FCSTD DOCUMENT  (FreeCAD 0.19R24291 (Git))
Label: assembly
License: All rights reserved
LicenseURL: http://en.wikipedia.org/wiki/All_rights_reserved
objects: App::Link×9, App::DocumentObjectGroup×3, PartDesign::CoordinateSystem×1, App::FeaturePython×1, App::Part×1
note: 1 computed .brp shape members not serialized (recipe doc carries the construction recipe); baked Part::Feature solids carry a one-line shape summary decoded from their .brp
EXTERNAL_REF file=Back.FCStd obj=LCS_0
EXTERNAL_REF file=Back.FCStd obj=Body_back
EXTERNAL_REF file=Back.FCStd obj=LCS_gear02
EXTERNAL_REF file=Gear02.FCStd obj=LCS_0
EXTERNAL_REF file=Gear02.FCStd obj=Part_gear02
EXTERNAL_REF file=Back.FCStd obj=LCS_stepper_mount_1
EXTERNAL_REF file=Stepper28BYJ48.FCStd obj=LCS_mount2
EXTERNAL_REF file=Stepper28BYJ48.FCStd obj=Part_Stepper28BYJ48
EXTERNAL_REF file=Gear01.FCStd obj=LCS_0
EXTERNAL_REF file=Stepper28BYJ48.FCStd obj=LCS_gear01
EXTERNAL_REF file=Gear01.FCStd obj=Part_gear01
EXTERNAL_REF file=Back.FCStd obj=LCS_spacer
EXTERNAL_REF file=Gear02Cap.FCStd obj=LCS_0
EXTERNAL_REF file=Gear02Cap.FCStd obj=Body_gear02cap
EXTERNAL_REF file=Back.FCStd obj=LCS_lcd
EXTERNAL_REF file=LCD114.FCStd obj=LCS_mount
EXTERNAL_REF file=LCD114.FCStd obj=Body_lcd1_14
EXTERNAL_REF file=Back.FCStd obj=LCS_pcb_1
EXTERNAL_REF file=PCB.FCStd obj=LCS_0
EXTERNAL_REF file=PCB.FCStd obj=Board_18fc
EXTERNAL_REF file=Back.FCStd obj=LCS_front
EXTERNAL_REF file=Front.FCStd obj=LCS_back
EXTERNAL_REF file=Front.FCStd obj=Body_front
EXTERNAL_REF file=PCB.FCStd obj=LCS_knob
EXTERNAL_REF file=knob.FCStd obj=LCS_encoder
EXTERNAL_REF file=knob.FCStd obj=Body_knob

FEATURE [App::DocumentObjectGroup] Parts
FEATURE [PartDesign::CoordinateSystem] LCS_Origin
  AttacherType = Attacher::AttachEngine3D
  MapMode = 2
  Support = -> [X_Axis]
FEATURE [App::FeaturePython] Variables  # WARN: FeaturePython — macro-defined, semantics opaque (R4)
  Type = App::PropertyContainer
FEATURE [App::DocumentObjectGroup] Constraints
FEATURE [App::DocumentObjectGroup] Configurations
FEATURE [App::Link] Body_back
  AttachedBy = #LCS_0
  AttachedTo = Parent Assembly#LCS_Origin
  LinkedObject = -> <external Back.FCStd>#Body_back
  SolverId = Placement::ExpressionEngine
  expr: Placement = LCS_Origin.Placement * AttachmentOffset * Back#LCS_0.Placement ^ -1
FEATURE [App::Link] Part_gear02
  AttachedBy = #LCS_0
  AttachedTo = Body_back#LCS_gear02
  AttachmentOffset = pos=(0,0,0) rot=(0,0,1;3.14159rad)
  LinkPlacement = pos=(17.15,53,27.8) rot=(0,0,1;4.71239rad)
  LinkedObject = -> <external Gear02.FCStd>#Part_gear02
  Placement = pos=(17.15,53,27.8) rot=(0,0,1;4.71239rad)
  SolverId = Placement::ExpressionEngine
  expr: Placement = Body_back.Placement * Back#LCS_gear02.Placement * AttachmentOffset * Gear02#LCS_0.Placement ^ -1
FEATURE [App::Link] Part_Stepper28BYJ48
  AttachedBy = #LCS_mount2
  AttachedTo = Body_back#LCS_stepper_mount_1
  AttachmentOffset = pos=(0,0,0) rot=(0.707107,0.707107,0;3.14159rad)
  LinkPlacement = pos=(-13.35,53,6.9) rot=(-0.57735,0.57735,0.57735;4.18879rad)
  LinkedObject = -> <external Stepper28BYJ48.FCStd>#Part_Stepper28BYJ48
  Placement = pos=(-13.35,53,6.9) rot=(-0.57735,0.57735,0.57735;4.18879rad)
  SolverId = Placement::ExpressionEngine
  expr: Placement = Body_back.Placement * Back#LCS_stepper_mount_1.Placement * AttachmentOffset * Stepper28BYJ48#LCS_mount2.Placement ^ -1
FEATURE [App::Link] Part_gear01
  AttachedBy = #LCS_0
  AttachedTo = Part_Stepper28BYJ48#LCS_gear01
  AttachmentOffset = pos=(0,0,0) rot=(0,0,1;1.5708rad)
  LinkPlacement = pos=(-5.35,53,27.4) rot=(0,0,1;0rad)
  LinkedObject = -> <external Gear01.FCStd>#Part_gear01
  Placement = pos=(-5.35,53,27.4) rot=(0,0,1;0rad)
  SolverId = Placement::ExpressionEngine
  expr: Placement = Part_Stepper28BYJ48.Placement * Stepper28BYJ48#LCS_gear01.Placement * AttachmentOffset * Gear01#LCS_0.Placement ^ -1
FEATURE [App::Link] Body_gear02cap
  AttachedBy = #LCS_0
  AttachedTo = Body_back#LCS_spacer
  LinkPlacement = pos=(17.15,53,35) rot=(0,0,1;1.5708rad)
  LinkedObject = -> <external Gear02Cap.FCStd>#Body_gear02cap
  Placement = pos=(17.15,53,35) rot=(0,0,1;1.5708rad)
  SolverId = Placement::ExpressionEngine
  expr: Placement = Body_back.Placement * Back#LCS_spacer.Placement * AttachmentOffset * Gear02Cap#LCS_0.Placement ^ -1
FEATURE [App::Link] Body_LCD114
  AttachedBy = #LCS_mount
  AttachedTo = Body_back#LCS_lcd
  AttachmentOffset = pos=(0,0,0) rot=(0,0,1;3.14159rad)
  LinkPlacement = pos=(-5.3e-15,-58.5,46.25) rot=(0,0,1;3.14159rad)
  LinkedObject = -> <external LCD114.FCStd>#Body_lcd1_14
  Placement = pos=(-5.3e-15,-58.5,46.25) rot=(0,0,1;3.14159rad)
  SolverId = Placement::ExpressionEngine
  expr: Placement = Body_back.Placement * Back#LCS_lcd.Placement * AttachmentOffset * LCD114#LCS_mount.Placement ^ -1
FEATURE [App::Link] PCB
  AttachedBy = #LCS_0
  AttachedTo = Body_back#LCS_pcb_1
  LinkPlacement = pos=(-39.15,-25.3,38.6) rot=(0,0,1;0rad)
  LinkedObject = -> <external PCB.FCStd>#Board_18fc
  Placement = pos=(-39.15,-25.3,38.6) rot=(0,0,1;0rad)
  SolverId = Placement::ExpressionEngine
  expr: Placement = Body_back.Placement * Back#LCS_pcb_1.Placement * AttachmentOffset * PCB#LCS_0.Placement ^ -1
FEATURE [App::Link] Body_front
  AttachedBy = #LCS_back
  AttachedTo = Body_back#LCS_front
  AttachmentOffset = pos=(0,0,0) rot=(0,0,1;3.14159rad)
  LinkPlacement = pos=(-1.066e-13,2.487e-13,49.6) rot=(0,0,1;0rad)
  LinkedObject = -> <external Front.FCStd>#Body_front
  Placement = pos=(-1.066e-13,2.487e-13,49.6) rot=(0,0,1;0rad)
  SolverId = Placement::ExpressionEngine
  expr: Placement = Body_back.Placement * Back#LCS_front.Placement * AttachmentOffset * Front#LCS_back.Placement ^ -1
FEATURE [App::Link] Body_knob
  AttachedBy = #LCS_encoder
  AttachedTo = PCB#LCS_knob
  AttachmentOffset = pos=(0,0,0) rot=(1,0,0;3.14159rad)
  LinkPlacement = pos=(-7.05,1.6,46.4) rot=(0,0,1;3.72602rad)
  LinkedObject = -> <external knob.FCStd>#Body_knob
  Placement = pos=(-7.05,1.6,46.4) rot=(0,0,1;3.72602rad)
  SolverId = Placement::ExpressionEngine
  expr: Placement = PCB.Placement * PCB#LCS_knob.Placement * AttachmentOffset * knob#LCS_encoder.Placement ^ -1
FEATURE [App::Part] Assembly
  AssemblyType = Part::Link
  Group = -> [LCS_Origin,Variables,Constraints,Configurations,Body_back,Part_gear02,Part_Stepper28BYJ48,Part_gear01,Body_gear02cap,Body_LCD114,PCB,Body_front,Body_knob]
  Origin = -> Origin
  Type = Assembly

RESOLVED EXTERNAL PARTS (link-assembly join: the EXTERNAL_REF files above that resolve inside this repo's crawl, each included once):
---- part Back.FCStd = doc fcstd_51bf11bdf407 ----
FCSTD DOCUMENT  (FreeCAD 0.19R24291 (Git))
Label: Back
License: All rights reserved
LicenseURL: http://en.wikipedia.org/wiki/All_rights_reserved
objects: Sketcher::SketchObject×9, PartDesign::Pad×9, PartDesign::CoordinateSystem×7, PartDesign::Fillet×1, PartDesign::Body×1
note: 37 computed .brp shape members not serialized (recipe doc carries the construction recipe); baked Part::Feature solids carry a one-line shape summary decoded from their .brp
EXTERNAL_REF file=data.FCStd obj=Spreadsheet

FEATURE [PartDesign::CoordinateSystem] LCS_0
  AttacherType = Attacher::AttachEngine3D
  MapMode = 2
  Support = -> [X_Axis]
FEATURE [Sketcher::SketchObject] Sketch  label="Sketch_back"
  FullyConstrained = true
  MapMode = 5
  Support = -> [XY_Plane]
  expr: Constraints[27] = data#<<data>>.OutsideLength
  expr: Constraints[28] = data#<<data>>.OutsideRadius
  expr: Constraints[26] = data#<<data>>.OutsideWidth
  expr: Constraints[25] = data#<<data>>.OutsideCornerRadius
  sketch-geometry (12):
    g0: ArcOfCircle CenterX=-37.75 CenterY=73.6 CenterZ=0 NormalX=0 NormalY=0 NormalZ=1 AngleXU=0 Radius=4.8 StartAngle=1.5708 EndAngle=3.14159
    g1: ArcOfCircle CenterX=17.15 CenterY=53 CenterZ=0 NormalX=0 NormalY=0 NormalZ=1 AngleXU=0 Radius=25.4 StartAngle=0 EndAngle=1.5708
    g2: ArcOfCircle CenterX=37.75 CenterY=-73.6 CenterZ=0 NormalX=0 NormalY=0 NormalZ=1 AngleXU=0 Radius=4.8 StartAngle=4.71239 EndAngle=6.28319
    g3: ArcOfCircle CenterX=-37.75 CenterY=-73.6 CenterZ=0 NormalX=0 NormalY=0 NormalZ=1 AngleXU=0 Radius=4.8 StartAngle=3.14159 EndAngle=4.71239
    g4: LineSegment StartX=-42.55 StartY=73.6 StartZ=0 EndX=-42.55 EndY=78.4 EndZ=0
    g5: LineSegment StartX=-37.75 StartY=78.4 StartZ=0 EndX=-42.55 EndY=78.4 EndZ=0
    g6: LineSegment StartX=37.75 StartY=-78.4 StartZ=0 EndX=42.55 EndY=-78.4 EndZ=0
    g7: LineSegment StartX=42.55 StartY=-73.6 StartZ=0 EndX=42.55 EndY=-78.4 EndZ=0
    g8: LineSegment StartX=-42.55 StartY=73.6 StartZ=0 EndX=-42.55 EndY=-73.6 EndZ=0
    g9: LineSegment StartX=-37.75 StartY=78.4 StartZ=0 EndX=17.15 EndY=78.4 EndZ=0
    g10: LineSegment StartX=42.55 StartY=53 StartZ=0 EndX=42.55 EndY=-73.6 EndZ=0
    g11: LineSegment StartX=-37.75 StartY=-78.4 StartZ=0 EndX=37.75 EndY=-78.4 EndZ=0
  constraints (37):
    c: Equal(g0,g3)
    c: Equal(g3,g2)
    c: Vertical(g0,g0)
    c: Vertical(g3,g3)
    c: Vertical(g2,g2)
    c: Vertical(g1,g1)
    c: Horizontal(g0,g0)
    c: Horizontal(g1,g1)
    c: Horizontal(g2,g2)
    c: Horizontal(g3,g3)
    c: Vertical(g0,g3)
    c: Vertical(g1,g2)
    c: Horizontal(g0,g1)
    c: Horizontal(g3,g2)
    c: Coincident(g4,g0)
    c: Vertical(g4)
    c: Coincident(g5,g0)
    c: Horizontal(g5)
    c: Coincident(g6,g2)
    c: Horizontal(g6)
    c: Coincident(g7,g2)
    c: Vertical(g7)
    c: Coincident(g5,g4)
    c: Coincident(g7,g6)
    c: Symmetric(g4,g6,g-1)
    c: Radius(g3) = 4.8
    c: DistanceX(g4,g1) = 85.1
    c: DistanceY(g3,g4) = 156.8
    c: Radius(g1) = 25.4
    c: Coincident(g8,g0)
    c: Coincident(g9,g0)
    c: Coincident(g10,g1)
    c: Coincident(g11,g3)
    c: Coincident(g11,g2)
    c: Coincident(g2,g10)
    c: Coincident(g8,g3)
    c: Coincident(g9,g1)
FEATURE [PartDesign::Pad] Pad
  Direction = (1,1,1)
  Length = 2.4
  Length2 = 100
  Profile = -> Sketch
  Type = 0
  expr: Length = data#<<data>>.WallThickness
FEATURE [Sketcher::SketchObject] Sketch001  label="Sketch_wall1"
  AttachmentOffset = pos=(0,0,2.4) rot=(0,0,1;0rad)
  FullyConstrained = true
  MapMode = 5
  Placement = pos=(0,0,2.4) rot=(0,0,1;0rad)
  Support = -> [XY_Plane]
  expr: Constraints[48] = data#<<data>>.InsideRadius
  expr: Constraints[47] = data#<<data>>.InsideCornerRadius
  expr: .AttachmentOffset.Base.z = data#<<data>>.WallThickness
  expr: Constraints[24] = data#<<data>>.OutsideWidth
  expr: Constraints[22] = data#<<data>>.OutsideRadius
  expr: Constraints[23] = data#<<data>>.OutsideLength
  expr: Constraints[21] = data#<<data>>.OutsideCornerRadius
  sketch-geometry (20):
    g0: ArcOfCircle CenterX=-37.75 CenterY=73.6 CenterZ=0 NormalX=0 NormalY=0 NormalZ=1 AngleXU=0 Radius=4.8 StartAngle=1.5708 EndAngle=3.14159
    g1: ArcOfCircle CenterX=17.15 CenterY=53 CenterZ=0 NormalX=0 NormalY=0 NormalZ=1 AngleXU=0 Radius=25.4 StartAngle=0 EndAngle=1.5708
    g2: ArcOfCircle CenterX=37.75 CenterY=-73.6 CenterZ=0 NormalX=0 NormalY=0 NormalZ=1 AngleXU=0 Radius=4.8 StartAngle=4.71239 EndAngle=6.28319
    g3: ArcOfCircle CenterX=-37.75 CenterY=-73.6 CenterZ=0 NormalX=0 NormalY=0 NormalZ=1 AngleXU=0 Radius=4.8 StartAngle=3.14159 EndAngle=4.71239
    g4: LineSegment StartX=-42.55 StartY=73.6 StartZ=0 EndX=-42.55 EndY=78.4 EndZ=0
    g5: LineSegment StartX=-37.75 StartY=78.4 StartZ=0 EndX=-42.55 EndY=78.4 EndZ=0
    g6: LineSegment StartX=37.75 StartY=-78.4 StartZ=0 EndX=42.55 EndY=-78.4 EndZ=0
    g7: LineSegment StartX=42.55 StartY=-73.6 StartZ=0 EndX=42.55 EndY=-78.4 EndZ=0
    g8: LineSegment StartX=-42.55 StartY=73.6 StartZ=0 EndX=-42.55 EndY=-73.6 EndZ=0
    g9: LineSegment StartX=-37.75 StartY=78.4 StartZ=0 EndX=17.15 EndY=78.4 EndZ=0
    g10: LineSegment StartX=42.55 StartY=53 StartZ=0 EndX=42.55 EndY=-73.6 EndZ=0
    g11: LineSegment StartX=37.75 StartY=-78.4 StartZ=0 EndX=-37.75 EndY=-78.4 EndZ=0
    g12: ArcOfCircle CenterX=-37.75 CenterY=73.6 CenterZ=0 NormalX=0 NormalY=0 NormalZ=1 AngleXU=0 Radius=2.4 StartAngle=1.5708 EndAngle=3.14159
    g13: ArcOfCircle CenterX=17.15 CenterY=53 CenterZ=0 NormalX=0 NormalY=0 NormalZ=1 AngleXU=0 Radius=23 StartAngle=0 EndAngle=1.5708
    g14: ArcOfCircle CenterX=37.75 CenterY=-73.6 CenterZ=0 NormalX=0 NormalY=0 NormalZ=1 AngleXU=0 Radius=2.4 StartAngle=4.71239 EndAngle=6.28319
    g15: ArcOfCircle CenterX=-37.75 CenterY=-73.6 CenterZ=0 NormalX=0 NormalY=0 NormalZ=1 AngleXU=0 Radius=2.4 StartAngle=3.14159 EndAngle=4.71239
    g16: LineSegment StartX=-37.75 StartY=76 StartZ=0 EndX=17.15 EndY=76 EndZ=0
    g17: LineSegment StartX=40.15 StartY=53 StartZ=0 EndX=40.15 EndY=-73.6 EndZ=0
    g18: LineSegment StartX=37.75 StartY=-76 StartZ=0 EndX=-37.75 EndY=-76 EndZ=0
    g19: LineSegment StartX=-40.15 StartY=-73.6 StartZ=0 EndX=-40.15 EndY=73.6 EndZ=0
  constraints (61):
    c: Vertical(g0,g0)
    c: Vertical(g1,g1)
    c: Vertical(g2,g2)
    c: Vertical(g3,g3)
    c: Horizontal(g0,g0)
    c: Horizontal(g1,g1)
    c: Horizontal(g3,g3)
    c: Horizontal(g2,g2)
    c: Coincident(g4,g0)
    c: Vertical(g4)
    c: Coincident(g5,g0)
    c: Horizontal(g5)
    c: Coincident(g4,g5)
    c: Equal(g3,g2)
    c: Equal(g2,g0)
    c: Coincident(g6,g2)
    c: Horizontal(g6)
    c: Coincident(g7,g2)
    c: Vertical(g7)
    c: Coincident(g7,g6)
    c: Symmetric(g4,g6,g-1)
    c: Radius(g3) = 4.8
    c: Radius(g1) = 25.4
    c: DistanceY(g3,g4) = 156.8
    c: DistanceX(g4,g1) = 85.1
    c: Vertical(g0,g3)
    c: Vertical(g1,g2)
    c: Horizontal(g0,g1)
    c: Horizontal(g3,g2)
    c: Coincident(g8,g0)
    c: Coincident(g8,g3)
    c: Coincident(g9,g0)
    c: Coincident(g9,g1)
    c: Coincident(g10,g1)
    c: Coincident(g10,g2)
    c: Coincident(g11,g2)
    c: Coincident(g11,g3)
    c: Vertical(g12,g12)
    c: Vertical(g13,g13)
    c: Horizontal(g12,g12)
    c: Horizontal(g13,g13)
    c: Horizontal(g14,g14)
    c: Horizontal(g15,g15)
    c: Vertical(g15,g15)
    c: Vertical(g14,g14)
    c: Equal(g12,g15)
    c: Equal(g15,g14)
    c: Radius(g15) = 2.4
    c: Radius(g13) = 23
    c: Coincident(g13,g1)
    c: Coincident(g12,g0)
    c: Coincident(g15,g3)
    c: Coincident(g14,g2)
    c: Coincident(g16,g12)
    c: Coincident(g16,g13)
    c: Coincident(g17,g13)
    c: Coincident(g17,g14)
    c: Coincident(g18,g14)
    c: Coincident(g18,g15)
    c: Coincident(g19,g15)
    c: Coincident(g19,g12)
FEATURE [PartDesign::Pad] Pad001
  BaseFeature = -> Pad
  Direction = (1,1,1)
  Length = 25.2
  Length2 = 100
  Profile = -> Sketch001
  Type = 0
  expr: Length = data#<<data>>.Gear02Height - data#<<data>>.Gear02Tol
FEATURE [Sketcher::SketchObject] Sketch002  label="Sketch_stepper_mount"
  AttachmentOffset = pos=(0,0,2.4) rot=(0,0,1;0rad)
  FullyConstrained = true
  MapMode = 5
  Placement = pos=(0,0,2.4) rot=(0,0,1;0rad)
  Support = -> [XY_Plane]
  expr: Constraints[23] = data#<<data>>.StepperMountOutsideDiameter
  expr: Constraints[20] = data#<<data>>.Gear02Dist
  expr: Constraints[19] = data#<<data>>.StepperMountWidth
  expr: Constraints[28] = data#<<data>>.M4DiameterTap
  expr: Constraints[14] = data#<<data>>.InsideLength
  expr: Constraints[13] = data#<<data>>.InsideWidth
  expr: Constraints[12] = data#<<data>>.InsideRadius
  expr: .AttachmentOffset.Base.z = data#<<data>>.WallThickness
  sketch-geometry (11):
    g0: LineSegment StartX=-40.15 StartY=76 StartZ=0 EndX=17.15 EndY=76 EndZ=0
    g1: LineSegment StartX=40.15 StartY=53 StartZ=0 EndX=40.15 EndY=-76 EndZ=0
    g2: LineSegment StartX=40.15 StartY=-76 StartZ=0 EndX=-40.15 EndY=-76 EndZ=0
    g3: LineSegment StartX=-40.15 StartY=-76 StartZ=0 EndX=-40.15 EndY=76 EndZ=0
    g4: ArcOfCircle CenterX=17.15 CenterY=53 CenterZ=0 NormalX=0 NormalY=0 NormalZ=1 AngleXU=0 Radius=23 StartAngle=0 EndAngle=1.5708
    g5: LineSegment StartX=17.15 StartY=53 StartZ=0 EndX=-13.35 EndY=53 EndZ=0
    g6: LineSegment StartX=-13.35 StartY=70.5 StartZ=0 EndX=-13.35 EndY=35.5 EndZ=0
    g7: Circle CenterX=-13.35 CenterY=70.5 CenterZ=0 NormalX=0 NormalY=0 NormalZ=1 AngleXU=0 Radius=3.5
    g8: Circle CenterX=-13.35 CenterY=35.5 CenterZ=0 NormalX=0 NormalY=0 NormalZ=1 AngleXU=0 Radius=3.5
    g9: Circle CenterX=-13.35 CenterY=70.5 CenterZ=0 NormalX=0 NormalY=0 NormalZ=1 AngleXU=0 Radius=1.9
    g10: Circle CenterX=-13.35 CenterY=35.5 CenterZ=0 NormalX=0 NormalY=0 NormalZ=1 AngleXU=0 Radius=1.9
  constraints (29):
    c: Coincident(g1,g2)
    c: Coincident(g2,g3)
    c: Coincident(g3,g0)
    c: Horizontal(g0)
    c: Horizontal(g2)
    c: Vertical(g1)
    c: Vertical(g3)
    c: Symmetric(g0,g1,g-1)
    c: Vertical(g4,g4)
    c: Horizontal(g4,g4)
    c: Coincident(g4,g0)
    c: Coincident(g4,g1)
    c: Radius(g4) = 23
    c: DistanceX(g2,g2) = 80.3
    c: DistanceY(g3,g3) = 152
    c: Coincident(g5,g4)
    c: Horizontal(g5)
    c: Vertical(g6)
    c: Symmetric(g6,g6,g5)
    c: DistanceY(g6,g6) = 35
    c: DistanceX(g5,g5) = 30.5
    c: Coincident(g7,g6)
    c: Coincident(g8,g6)
    c: Diameter(g7) = 7
    c: Equal(g7,g8)
    c: Coincident(g9,g7)
    c: Coincident(g10,g8)
    c: Equal(g9,g10)
    c: Diameter(g10) = 3.8
FEATURE [PartDesign::Pad] Pad002
  BaseFeature = -> Pad001
  Direction = (1,1,1)
  Length = 23
  Length2 = 100
  Profile = -> Sketch002
  Type = 0
  expr: Length = data#<<data>>.StepperMountHeight
FEATURE [Sketcher::SketchObject] Sketch003  label="Sketch_gear02_mount"
  AttachmentOffset = pos=(0,0,2.4) rot=(0,0,1;0rad)
  FullyConstrained = true
  MapMode = 5
  Placement = pos=(0,0,2.4) rot=(0,0,1;0rad)
  Support = -> [XY_Plane]
  expr: Constraints[18] = data#<<data>>.M3DiameterTap
  expr: Constraints[16] = data#<<data>>.Gear02MountDiameter
  expr: .AttachmentOffset.Base.z = data#<<data>>.WallThickness
  expr: Constraints[12] = data#<<data>>.InsideRadius
  expr: Constraints[13] = data#<<data>>.InsideWidth
  expr: Constraints[14] = data#<<data>>.InsideLength
  sketch-geometry (7):
    g0: LineSegment StartX=-40.15 StartY=76 StartZ=0 EndX=17.15 EndY=76 EndZ=0
    g1: LineSegment StartX=40.15 StartY=53 StartZ=0 EndX=40.15 EndY=-76 EndZ=0
    g2: LineSegment StartX=40.15 StartY=-76 StartZ=0 EndX=-40.15 EndY=-76 EndZ=0
    g3: LineSegment StartX=-40.15 StartY=-76 StartZ=0 EndX=-40.15 EndY=76 EndZ=0
    g4: ArcOfCircle CenterX=17.15 CenterY=53 CenterZ=0 NormalX=0 NormalY=0 NormalZ=1 AngleXU=0 Radius=23 StartAngle=0 EndAngle=1.5708
    g5: Circle CenterX=17.15 CenterY=53 CenterZ=0 NormalX=0 NormalY=0 NormalZ=1 AngleXU=0 Radius=5
    g6: Circle CenterX=17.15 CenterY=53 CenterZ=0 NormalX=0 NormalY=0 NormalZ=1 AngleXU=0 Radius=1.4
  constraints (19):
    c: Coincident(g1,g2)
    c: Coincident(g2,g3)
    c: Coincident(g3,g0)
    c: Horizontal(g0)
    c: Horizontal(g2)
    c: Vertical(g1)
    c: Vertical(g3)
    c: Symmetric(g0,g1,g-1)
    c: Vertical(g4,g4)
    c: Horizontal(g4,g4)
    c: Coincident(g4,g0)
    c: Coincident(g4,g1)
    c: Radius(g4) = 23
    c: DistanceX(g2,g2) = 80.3
    c: DistanceY(g3,g3) = 152
    c: Coincident(g5,g4)
    c: Diameter(g5) = 10
    c: Coincident(g6,g5)
    c: Diameter(g6) = 2.8
FEATURE [PartDesign::Pad] Pad003
  BaseFeature = -> Pad002
  Direction = (1,1,1)
  Length = 25.4
  Length2 = 100
  Profile = -> Sketch003
  Type = 0
  expr: Length = data#<<data>>.Gear02Height
FEATURE [Sketcher::SketchObject] Sketch004  label="Sketch_gear02_shaft"
  AttachmentOffset = pos=(0,0,27.8) rot=(0,0,1;0rad)
  FullyConstrained = true
  MapMode = 5
  Placement = pos=(0,0,27.8) rot=(0,0,1;0rad)
  Support = -> [XY_Plane]
  expr: Constraints[14] = data#<<data>>.InsideLength
  expr: Constraints[13] = data#<<data>>.InsideWidth
  expr: Constraints[12] = data#<<data>>.InsideRadius
  expr: .AttachmentOffset.Base.z = data#<<data>>.WallThickness + data#<<data>>.Gear02Height
  expr: Constraints[18] = data#<<data>>.M3DiameterTap
  expr: Constraints[16] = data#<<data>>.Gear02ShaftDiameter
  sketch-geometry (7):
    g0: LineSegment StartX=-40.15 StartY=76 StartZ=0 EndX=17.15 EndY=76 EndZ=0
    g1: LineSegment StartX=40.15 StartY=53 StartZ=0 EndX=40.15 EndY=-76 EndZ=0
    g2: LineSegment StartX=40.15 StartY=-76 StartZ=0 EndX=-40.15 EndY=-76 EndZ=0
    g3: LineSegment StartX=-40.15 StartY=-76 StartZ=0 EndX=-40.15 EndY=76 EndZ=0
    g4: ArcOfCircle CenterX=17.15 CenterY=53 CenterZ=0 NormalX=0 NormalY=0 NormalZ=1 AngleXU=0 Radius=23 StartAngle=0 EndAngle=1.5708
    g5: Circle CenterX=17.15 CenterY=53 CenterZ=0 NormalX=0 NormalY=0 NormalZ=1 AngleXU=0 Radius=3
    g6: Circle CenterX=17.15 CenterY=53 CenterZ=0 NormalX=0 NormalY=0 NormalZ=1 AngleXU=0 Radius=1.4
  constraints (19):
    c: Coincident(g1,g2)
    c: Coincident(g2,g3)
    c: Coincident(g3,g0)
    c: Horizontal(g0)
    c: Horizontal(g2)
    c: Vertical(g1)
    c: Vertical(g3)
    c: Symmetric(g0,g1,g-1)
    c: Vertical(g4,g4)
    c: Horizontal(g4,g4)
    c: Coincident(g4,g0)
    c: Coincident(g4,g1)
    c: Radius(g4) = 23
    c: DistanceX(g2,g2) = 80.3
    c: DistanceY(g3,g3) = 152
    c: Coincident(g5,g4)
    c: Diameter(g5) = 6
    c: Coincident(g6,g5)
    c: Diameter(g6) = 2.8
FEATURE [PartDesign::Pad] Pad004
  BaseFeature = -> Pad003
  Direction = (1,1,1)
  Length = 7.2
  Length2 = 100
  Profile = -> Sketch004
  Type = 0
  expr: Length = data#<<data>>.Gear02ShaftLength
FEATURE [Sketcher::SketchObject] Sketch005  label="Sketch_pcb_mount"
  AttachmentOffset = pos=(0,0,2.4) rot=(0,0,1;0rad)
  FullyConstrained = true
  MapMode = 5
  Placement = pos=(0,0,2.4) rot=(0,0,1;0rad)
  Support = -> [XY_Plane]
  expr: .AttachmentOffset.Base.z = data#<<data>>.WallThickness
  expr: Constraints[39] = data#<<data>>.KnobShaftOffsetX - data#<<data>>.WallThickness
  expr: Constraints[5] = data#<<data>>.InsideRadius
  expr: Constraints[38] = data#<<data>>.KnobShaftOffsetY - data#<<data>>.WallThickness
  expr: Constraints[13] = data#<<data>>.InsideWidth
  expr: Constraints[14] = data#<<data>>.InsideLength
  expr: Constraints[26] = data#<<data>>.PCBMountY
  expr: Constraints[25] = data#<<data>>.PCBMountY
  expr: Constraints[29] = data#<<data>>.PCBMount1X
  expr: Constraints[27] = data#<<data>>.PCBMount2X
  expr: Constraints[30] = data#<<data>>.PCBMountOutsideDiameter
  expr: Constraints[23] = data#<<data>>.PCBLength
  expr: Constraints[32] = data#<<data>>.PCBGear02Y
  expr: Constraints[24] = data#<<data>>.PCBWidth
  expr: Constraints[31] = data#<<data>>.PCBGear02X
  expr: Constraints[36] = data#<<data>>.PCBMountInsideDiameter
  sketch-geometry (14):
    g0: LineSegment StartX=-40.15 StartY=76 StartZ=0 EndX=-40.15 EndY=-76 EndZ=0
    g1: LineSegment StartX=-40.15 StartY=-76 StartZ=0 EndX=40.15 EndY=-76 EndZ=0
    g2: LineSegment StartX=-40.15 StartY=76 StartZ=0 EndX=17.15 EndY=76 EndZ=0
    g3: ArcOfCircle CenterX=17.15 CenterY=53 CenterZ=0 NormalX=0 NormalY=0 NormalZ=1 AngleXU=0 Radius=23 StartAngle=0 EndAngle=1.5708
    g4: LineSegment StartX=40.15 StartY=53 StartZ=0 EndX=40.15 EndY=-76 EndZ=0
    g5: LineSegment StartX=-39.15 StartY=74.7 StartZ=0 EndX=20.85 EndY=74.7 EndZ=0
    g6: LineSegment StartX=20.85 StartY=74.7 StartZ=0 EndX=20.85 EndY=-25.3 EndZ=0
    g7: LineSegment StartX=20.85 StartY=-25.3 StartZ=0 EndX=-39.15 EndY=-25.3 EndZ=0
    g8: LineSegment StartX=-39.15 StartY=-25.3 StartZ=0 EndX=-39.15 EndY=74.7 EndZ=0
    g9: Circle CenterX=-23.15 CenterY=-20.3 CenterZ=0 NormalX=0 NormalY=0 NormalZ=1 AngleXU=0 Radius=3.5
    g10: Circle CenterX=15.85 CenterY=-20.3 CenterZ=0 NormalX=0 NormalY=0 NormalZ=1 AngleXU=0 Radius=3.5
    g11: Circle CenterX=-23.15 CenterY=-20.3 CenterZ=0 NormalX=0 NormalY=0 NormalZ=1 AngleXU=0 Radius=1.4
    g12: Circle CenterX=15.85 CenterY=-20.3 CenterZ=0 NormalX=0 NormalY=0 NormalZ=1 AngleXU=0 Radius=1.4
    g13: Circle CenterX=-7.55 CenterY=2.4 CenterZ=0 NormalX=0 NormalY=0 NormalZ=1 AngleXU=0 Radius=4
  constraints (40):
    c: Vertical(g0)
    c: Horizontal(g1)
    c: Horizontal(g2)
    c: Vertical(g3,g3)
    c: Horizontal(g3,g3)
    c: Radius(g3) = 23
    c: Coincident(g2,g3)
    c: Coincident(g2,g0)
    c: Coincident(g1,g0)
    c: Coincident(g4,g3)
    c: Vertical(g4)
    c: Coincident(g4,g1)
    c: Symmetric(g0,g1,g-1)
    c: DistanceX(g1,g1) = 80.3
    c: DistanceY(g0,g0) = 152
    c: Coincident(g5,g6)
    c: Coincident(g6,g7)
    c: Coincident(g7,g8)
    c: Coincident(g8,g5)
    c: Horizontal(g5)
    c: Horizontal(g7)
    c: Vertical(g6)
    c: Vertical(g8)
    c: DistanceY(g8,g8) = 100
    c: DistanceX(g5,g5) = 60
    c: DistanceY(g6,g10) = 5
    c: DistanceY(g7,g9) = 5
    c: DistanceX(g10,g6) = 5
    c: Equal(g9,g10)
    c: DistanceX(g7,g9) = 16
    c: Diameter(g10) = 7
    c: DistanceX(g3,g5) = 3.7
    c: DistanceY(g3,g5) = 21.7
    c: Coincident(g11,g9)
    c: Coincident(g12,g10)
    c: Equal(g11,g12)
    c: Diameter(g11) = 2.8
    c: Diameter(g13) = 8
    c: DistanceY(g13,g2) = 73.6
    c: DistanceX(g0,g13) = 32.6
FEATURE [PartDesign::Pad] Pad005
  BaseFeature = -> Pad004
  Direction = (1,1,1)
  Length = 34.6
  Length2 = 100
  Profile = -> Sketch005
  Type = 0
  expr: Length = data#<<data>>.PCBHeight
FEATURE [Sketcher::SketchObject] Sketch006  label="Sketch_wall2"
  AttachmentOffset = pos=(0,0,27.6) rot=(0,0,1;0rad)
  FullyConstrained = true
  MapMode = 5
  Placement = pos=(0,0,27.6) rot=(0,0,1;0rad)
  Support = -> [XY_Plane]
  expr: Constraints[39] = data#<<data>>.OutsideRadius
  expr: .AttachmentOffset.Base.z = data#<<data>>.Gear02Height - data#<<data>>.Gear02Tol + data#<<data>>.WallThickness
  expr: Constraints[40] = data#<<data>>.OutsideCornerRadius
  expr: Constraints[10] = data#<<data>>.InsideCornerRadius
  expr: Constraints[11] = data#<<data>>.InsideRadius
  expr: Constraints[20] = data#<<data>>.InsideWidth
  expr: Constraints[21] = data#<<data>>.InsideLength
  expr: Constraints[60] = data#<<data>>.OutsideLowAngle
  sketch-geometry (19):
    g0: ArcOfCircle CenterX=-37.75 CenterY=73.6 CenterZ=0 NormalX=0 NormalY=0 NormalZ=1 AngleXU=0 Radius=2.4 StartAngle=1.5708 EndAngle=3.14159
    g1: ArcOfCircle CenterX=17.15 CenterY=53 CenterZ=0 NormalX=0 NormalY=0 NormalZ=1 AngleXU=0 Radius=23 StartAngle=0 EndAngle=1.5708
    g2: ArcOfCircle CenterX=37.75 CenterY=-73.6 CenterZ=0 NormalX=0 NormalY=0 NormalZ=1 AngleXU=0 Radius=2.4 StartAngle=4.71239 EndAngle=6.28319
    g3: ArcOfCircle CenterX=-37.75 CenterY=-73.6 CenterZ=0 NormalX=0 NormalY=0 NormalZ=1 AngleXU=0 Radius=2.4 StartAngle=3.14159 EndAngle=4.71239
    g4: LineSegment StartX=-37.75 StartY=76 StartZ=0 EndX=17.15 EndY=76 EndZ=0
    g5: LineSegment StartX=-37.75 StartY=-76 StartZ=0 EndX=37.75 EndY=-76 EndZ=0
    g6: LineSegment StartX=-40.15 StartY=73.6 StartZ=0 EndX=-40.15 EndY=-73.6 EndZ=0
    g7: ArcOfCircle CenterX=-37.75 CenterY=73.6 CenterZ=0 NormalX=0 NormalY=0 NormalZ=1 AngleXU=0 Radius=4.8 StartAngle=1.5708 EndAngle=3.14159
    g8: ArcOfCircle CenterX=17.15 CenterY=53 CenterZ=0 NormalX=0 NormalY=0 NormalZ=1 AngleXU=0 Radius=25.4 StartAngle=0 EndAngle=1.5708
    g9: ArcOfCircle CenterX=37.75 CenterY=-73.6 CenterZ=0 NormalX=0 NormalY=0 NormalZ=1 AngleXU=0 Radius=4.8 StartAngle=4.71239 EndAngle=6.28319
    g10: ArcOfCircle CenterX=-37.75 CenterY=-73.6 CenterZ=0 NormalX=0 NormalY=0 NormalZ=1 AngleXU=0 Radius=4.8 StartAngle=3.14159 EndAngle=4.71239
    g11: LineSegment StartX=-42.55 StartY=73.6 StartZ=0 EndX=-42.55 EndY=-73.6 EndZ=0
    g12: LineSegment StartX=-37.75 StartY=-78.4 StartZ=0 EndX=37.75 EndY=-78.4 EndZ=0
    g13: LineSegment StartX=17.15 StartY=78.4 StartZ=0 EndX=-37.75 EndY=78.4 EndZ=0
    g14: LineSegment StartX=17.15 StartY=78.4 StartZ=0 EndX=17.15 EndY=76 EndZ=0
    g15: LineSegment StartX=40.15 StartY=-73.6 StartZ=0 EndX=40.15 EndY=31.6869 EndZ=0
    g16: LineSegment StartX=42.55 StartY=31.6869 StartZ=0 EndX=42.55 EndY=-73.6 EndZ=0
    g17: LineSegment StartX=40.15 StartY=31.6869 StartZ=0 EndX=42.55 EndY=31.6869 EndZ=0
    g18: LineSegment StartX=17.15 StartY=53 StartZ=0 EndX=42.55 EndY=31.6869 EndZ=0
  constraints (61):
    c: Vertical(g0,g0)
    c: Vertical(g3,g3)
    c: Vertical(g2,g2)
    c: Vertical(g1,g1)
    c: Horizontal(g1,g1)
    c: Horizontal(g2,g2)
    c: Horizontal(g3,g3)
    c: Horizontal(g0,g0)
    c: Equal(g0,g3)
    c: Equal(g3,g2)
    c: Radius(g3) = 2.4
    c: Radius(g1) = 23
    c: Vertical(g0,g3)
    c: Horizontal(g0,g1)
    c: Horizontal(g3,g2)
    c: Coincident(g4,g0)
    c: Coincident(g4,g1)
    c: Coincident(g5,g3)
    c: Coincident(g5,g2)
    c: Symmetric(g0,g2,g-1)
    c: DistanceX(g3,g2) = 80.3
    c: DistanceY(g3,g0) = 152
    c: Coincident(g6,g0)
    c: Coincident(g6,g3)
    c: Vertical(g7,g7)
    c: Vertical(g10,g10)
    c: Vertical(g8,g8)
    c: Vertical(g9,g9)
    c: Vertical(g8,g9)
    c: Vertical(g7,g10)
    c: Horizontal(g7,g7)
    c: Horizontal(g8,g8)
    c: Horizontal(g9,g9)
    c: Horizontal(g10,g10)
    c: Horizontal(g10,g9)
    c: Horizontal(g8,g7)
    c: Equal(g7,g10)
    c: Equal(g10,g9)
    c: Symmetric(g7,g9,g-1)
    c: Radius(g8) = 25.4
    c: Radius(g9) = 4.8
    c: Coincident(g11,g7)
    c: Coincident(g11,g10)
    c: Coincident(g12,g10)
    c: Coincident(g12,g9)
    c: Coincident(g13,g8)
    c: Coincident(g13,g7)
    c: Coincident(g10,g3)
    c: Vertical(g1,g2)
    c: Coincident(g14,g13)
    c: Coincident(g14,g4)
    c: Coincident(g15,g2)
    c: Vertical(g15)
    c: Vertical(g16)
    c: Coincident(g9,g16)
    c: Horizontal(g15,g16)
    c: Coincident(g17,g15)
    c: Coincident(g17,g16)
    c: Coincident(g18,g1)
    c: Coincident(g18,g16)
    c: Angle(g-2,g18) = 0.872665
FEATURE [PartDesign::Pad] Pad006
  BaseFeature = -> Pad005
  Direction = (1,1,1)
  Length = 11
  Length2 = 100
  Profile = -> Sketch006
  Type = 0
  expr: Length = data#<<data>>.Wall2Height
FEATURE [Sketcher::SketchObject] Sketch007  label="Sketch_wall3"
  AttachmentOffset = pos=(0,0,38.6) rot=(0,0,1;0rad)
  FullyConstrained = true
  MapMode = 5
  Placement = pos=(0,0,38.6) rot=(0,0,1;0rad)
  Support = -> [XY_Plane]
  expr: Constraints[11] = data#<<data>>.PCBWidth
  expr: Constraints[23] = data#<<data>>.InsideCornerRadius
  expr: Constraints[35] = data#<<data>>.InsideLength
  expr: Constraints[12] = data#<<data>>.PCBLength
  expr: Constraints[34] = data#<<data>>.InsideWidth
  expr: Constraints[13] = data#<<data>>.PCBGear02X
  expr: Constraints[82] = data#<<data>>.WallThickness
  expr: Constraints[44] = data#<<data>>.MiddleCornerRadius
  expr: Constraints[87] = data#<<data>>.OutsideLowAngle
  expr: .AttachmentOffset.Base.z = data#<<data>>.WallThickness + data#<<data>>.PCBHeight + data#<<data>>.PCBThickness
  expr: Constraints[51] = data#<<data>>.MiddleRadius
  expr: Constraints[73] = data#<<data>>.PCBPowerJackY
  expr: Constraints[14] = data#<<data>>.PCBGear02Y
  expr: Constraints[2] = data#<<data>>.InsideRadius
  expr: Constraints[74] = data#<<data>>.PowerJackWidth
  sketch-geometry (28):
    g0: ArcOfCircle CenterX=17.15 CenterY=53 CenterZ=0 NormalX=0 NormalY=0 NormalZ=1 AngleXU=0 Radius=23 StartAngle=0 EndAngle=1.5708
    g1: LineSegment StartX=-39.15 StartY=74.7 StartZ=0 EndX=20.85 EndY=74.7 EndZ=0
    g2: LineSegment StartX=20.85 StartY=74.7 StartZ=0 EndX=20.85 EndY=-25.3 EndZ=0
    g3: LineSegment StartX=20.85 StartY=-25.3 StartZ=0 EndX=-39.15 EndY=-25.3 EndZ=0
    g4: LineSegment StartX=-39.15 StartY=-25.3 StartZ=0 EndX=-39.15 EndY=74.7 EndZ=0
    g5: ArcOfCircle CenterX=-37.75 CenterY=73.6 CenterZ=0 NormalX=0 NormalY=0 NormalZ=1 AngleXU=0 Radius=2.4 StartAngle=1.5708 EndAngle=3.14159
    g6: ArcOfCircle CenterX=37.75 CenterY=-73.6 CenterZ=0 NormalX=0 NormalY=0 NormalZ=1 AngleXU=0 Radius=2.4 StartAngle=4.71239 EndAngle=6.28319
    g7: ArcOfCircle CenterX=-37.75 CenterY=-73.6 CenterZ=0 NormalX=0 NormalY=0 NormalZ=1 AngleXU=0 Radius=2.4 StartAngle=3.14159 EndAngle=4.71239
    g8: LineSegment StartX=-37.75 StartY=76 StartZ=0 EndX=17.15 EndY=76 EndZ=0
    g9: LineSegment StartX=40.15 StartY=31.6869 StartZ=0 EndX=40.15 EndY=-73.6 EndZ=0
    g10: LineSegment StartX=37.75 StartY=-76 StartZ=0 EndX=-37.75 EndY=-76 EndZ=0
    g11: ArcOfCircle CenterX=-37.75 CenterY=73.6 CenterZ=0 NormalX=0 NormalY=0 NormalZ=1 AngleXU=0 Radius=3.6 StartAngle=1.5708 EndAngle=3.14159
    g12: ArcOfCircle CenterX=-37.75 CenterY=-73.6 CenterZ=0 NormalX=0 NormalY=0 NormalZ=1 AngleXU=0 Radius=3.6 StartAngle=3.14159 EndAngle=4.71239
    g13: ArcOfCircle CenterX=37.75 CenterY=-73.6 CenterZ=0 NormalX=0 NormalY=0 NormalZ=1 AngleXU=0 Radius=3.6 StartAngle=4.71239 EndAngle=6.28319
    g14: ArcOfCircle CenterX=17.15 CenterY=53 CenterZ=0 NormalX=0 NormalY=0 NormalZ=1 AngleXU=0 Radius=24.2 StartAngle=0 EndAngle=1.5708
    g15: LineSegment StartX=-37.75 StartY=77.2 StartZ=0 EndX=17.15 EndY=77.2 EndZ=0
    g16: LineSegment StartX=41.35 StartY=31.6869 StartZ=0 EndX=41.35 EndY=-73.6 EndZ=0
    g17: LineSegment StartX=-37.75 StartY=-77.2 StartZ=0 EndX=37.75 EndY=-77.2 EndZ=0
    g18: LineSegment StartX=-41.35 StartY=-73.6 StartZ=0 EndX=-41.35 EndY=-19.55 EndZ=0
    g19: LineSegment StartX=-40.15 StartY=-73.6 StartZ=0 EndX=-40.15 EndY=-19.55 EndZ=0
    g20: LineSegment StartX=-41.35 StartY=73.6 StartZ=0 EndX=-41.35 EndY=-10.05 EndZ=0
    g21: LineSegment StartX=-40.15 StartY=73.6 StartZ=0 EndX=-40.15 EndY=-10.05 EndZ=0
    g22: LineSegment StartX=-41.35 StartY=-10.05 StartZ=0 EndX=-40.15 EndY=-10.05 EndZ=0
    g23: LineSegment StartX=-41.35 StartY=-19.55 StartZ=0 EndX=-40.15 EndY=-19.55 EndZ=0
    g24: LineSegment StartX=40.15 StartY=31.6869 StartZ=0 EndX=41.35 EndY=31.6869 EndZ=0
    g25: LineSegment StartX=41.35 StartY=31.6869 StartZ=0 EndX=42.55 EndY=31.6869 EndZ=0
    g26: LineSegment StartX=17.15 StartY=77.2 StartZ=0 EndX=17.15 EndY=76 EndZ=0
    g27: LineSegment StartX=17.15 StartY=53 StartZ=0 EndX=42.55 EndY=31.6869 EndZ=0
  constraints (88):
    c: Vertical(g0,g0)
    c: Horizontal(g0,g0)
    c: Radius(g0) = 23
    c: Coincident(g1,g2)
    c: Coincident(g2,g3)
    c: Coincident(g3,g4)
    c: Coincident(g4,g1)
    c: Horizontal(g1)
    c: Horizontal(g3)
    c: Vertical(g2)
    c: Vertical(g4)
    c: DistanceX(g1,g1) = 60
    c: DistanceY(g2,g2) = 100
    c: DistanceX(g0,g1) = 3.7
    c: DistanceY(g0,g1) = 21.7
    c: Vertical(g5,g5)
    c: Vertical(g7,g7)
    c: Vertical(g6,g6)
    c: Horizontal(g6,g6)
    c: Horizontal(g7,g7)
    c: Horizontal(g5,g5)
    c: Equal(g6,g7)
    c: Equal(g7,g5)
    c: Radius(g5) = 2.4
    c: Vertical(g0,g6)
    c: Vertical(g5,g7)
    c: Horizontal(g7,g6)
    c: Horizontal(g0,g5)
    c: Coincident(g8,g5)
    c: Coincident(g8,g0)
    c: Coincident(g9,g6)
    c: Coincident(g10,g6)
    c: Coincident(g10,g7)
    c: Symmetric(g5,g6,g-1)
    c: DistanceX(g7,g6) = 80.3
    c: DistanceY(g7,g5) = 152
    c: Vertical(g13,g13)
    c: Vertical(g12,g12)
    c: Vertical(g11,g11)
    c: Horizontal(g11,g11)
    c: Horizontal(g12,g12)
    c: Horizontal(g13,g13)
    c: Equal(g13,g12)
    c: Equal(g12,g11)
    c: Radius(g13) = 3.6
    c: Vertical(g14,g14)
    c: Horizontal(g14,g14)
    c: Vertical(g14,g13)
    c: Horizontal(g12,g13)
    c: Vertical(g12,g11)
    c: Horizontal(g11,g14)
    c: Radius(g14) = 24.2
    c: Symmetric(g11,g13,g-1)
    c: Coincident(g14,g0)
    c: Coincident(g15,g11)
    c: Coincident(g15,g14)
    c: Coincident(g16,g13)
    c: Coincident(g17,g12)
    c: Coincident(g17,g13)
    c: Coincident(g18,g12)
    c: Coincident(g19,g7)
    c: Coincident(g20,g11)
    c: Coincident(g21,g5)
    c: Vertical(g20)
    c: Vertical(g21)
    c: Vertical(g18)
    c: Vertical(g19)
    c: Horizontal(g18,g19)
    c: Horizontal(g20,g21)
    c: Coincident(g22,g20)
    c: Coincident(g22,g21)
    c: Coincident(g23,g18)
    c: Coincident(g23,g19)
    c: DistanceY(g3,g19) = 5.75
    c: DistanceY(g18,g20) = 9.5
    c: Horizontal(g9,g16)
    c: Vertical(g16)
    c: Vertical(g9)
    c: Coincident(g24,g9)
    c: Coincident(g24,g16)
    c: Coincident(g25,g16)
    c: Horizontal(g25)
    c: DistanceX(g9,g25) = 2.4
    c: Coincident(g26,g15)
    c: Coincident(g26,g8)
    c: Coincident(g27,g0)
    c: Coincident(g27,g25)
    c: Angle(g-2,g27) = 0.872665
FEATURE [PartDesign::Pad] Pad007
  BaseFeature = -> Pad006
  Direction = (1,1,1)
  Length = 11
  Length2 = 100
  Profile = -> Sketch007
  Type = 0
  expr: Length = data#<<data>>.Wall3Height
FEATURE [Sketcher::SketchObject] Sketch008  label="Sketch_lcd_mount"
  AttachmentOffset = pos=(0,0,2.4) rot=(0,0,1;0rad)
  FullyConstrained = true
  MapMode = 5
  Placement = pos=(0,0,2.4) rot=(0,0,1;0rad)
  Support = -> [XY_Plane]
  expr: .AttachmentOffset.Base.z = data#<<data>>.WallThickness
  expr: Constraints[11] = data#<<data>>.InsideRadius
  expr: Constraints[12] = data#<<data>>.InsideWidth
  expr: Constraints[31] = data#<<data>>.LCDMountOutsideDiameter
  expr: Constraints[13] = data#<<data>>.InsideLength
  expr: Constraints[28] = data#<<data>>.LCDMountDistY
  expr: Constraints[29] = data#<<data>>.LCDMountDistX
  expr: Constraints[30] = data#<<data>>.LCDMountInsideDiameter
  expr: Constraints[32] = data#<<data>>.LCDMountOffsetX
  expr: Constraints[33] = data#<<data>>.LCDMountOffsetY
  sketch-geometry (13):
    g0: ArcOfCircle CenterX=17.15 CenterY=53 CenterZ=0 NormalX=0 NormalY=0 NormalZ=1 AngleXU=0 Radius=23 StartAngle=0 EndAngle=1.5708
    g1: LineSegment StartX=17.15 StartY=76 StartZ=0 EndX=-40.15 EndY=76 EndZ=0
    g2: LineSegment StartX=-40.15 StartY=76 StartZ=0 EndX=-40.15 EndY=-76 EndZ=0
    g3: LineSegment StartX=-40.15 StartY=-76 StartZ=0 EndX=40.15 EndY=-76 EndZ=0
    g4: LineSegment StartX=40.15 StartY=-76 StartZ=0 EndX=40.15 EndY=53 EndZ=0
    g5: Circle CenterX=-15 CenterY=-45 CenterZ=0 NormalX=0 NormalY=0 NormalZ=1 AngleXU=0 Radius=1.4
    g6: Circle CenterX=-15 CenterY=-45 CenterZ=0 NormalX=0 NormalY=0 NormalZ=1 AngleXU=0 Radius=3.2
    g7: Circle CenterX=15 CenterY=-45 CenterZ=0 NormalX=0 NormalY=0 NormalZ=1 AngleXU=0 Radius=1.4
    g8: Circle CenterX=15 CenterY=-45 CenterZ=0 NormalX=0 NormalY=0 NormalZ=1 AngleXU=0 Radius=3.2
    g9: Circle CenterX=-15 CenterY=-72 CenterZ=0 NormalX=0 NormalY=0 NormalZ=1 AngleXU=0 Radius=1.4
    g10: Circle CenterX=-15 CenterY=-72 CenterZ=0 NormalX=0 NormalY=0 NormalZ=1 AngleXU=0 Radius=3.2
    g11: Circle CenterX=15 CenterY=-72 CenterZ=0 NormalX=0 NormalY=0 NormalZ=1 AngleXU=0 Radius=1.4
    g12: Circle CenterX=15 CenterY=-72 CenterZ=0 NormalX=0 NormalY=0 NormalZ=1 AngleXU=0 Radius=3.2
  constraints (34):
    c: Vertical(g0,g0)
    c: Horizontal(g0,g0)
    c: Tangent(g0,g1) = -1.5708
    c: Coincident(g1,g2)
    c: Vertical(g2)
    c: Coincident(g2,g3)
    c: Horizontal(g3)
    c: Coincident(g3,g4)
    c: Coincident(g4,g0)
    c: Vertical(g4)
    c: Symmetric(g3,g1,g-1)
    c: Radius(g0) = 23
    c: DistanceX(g3,g3) = 80.3
    c: DistanceY(g2,g2) = 152
    c: Coincident(g6,g5)
    c: Coincident(g8,g7)
    c: Coincident(g10,g9)
    c: Coincident(g12,g11)
    c: Equal(g5,g7)
    c: Equal(g7,g11)
    c: Equal(g11,g9)
    c: Equal(g6,g10)
    c: Equal(g10,g8)
    c: Equal(g8,g12)
    c: Horizontal(g5,g7)
    c: Horizontal(g9,g11)
    c: Vertical(g5,g9)
    c: Vertical(g7,g11)
    c: DistanceY(g9,g5) = 27
    c: DistanceX(g5,g7) = 30
    c: Diameter(g11) = 2.8
    c: Diameter(g12) = 6.4
    c: DistanceX(g2,g9) = 25.15
    c: DistanceY(g2,g9) = 4
FEATURE [PartDesign::Pad] Pad008
  BaseFeature = -> Pad007
  Direction = (1,1,1)
  Length = 43.85
  Length2 = 100
  Profile = -> Sketch008
  Type = 0
  expr: Length = data#<<data>>.LCDMountLength
FEATURE [PartDesign::Fillet] Fillet
  Base = -> Pad008 [Edge152,Edge153,Edge151,Edge147,Edge150,Edge149,Edge146,Edge145,Edge148,Edge154]
  BaseFeature = -> Pad008
  Radius = 2.4
  SupportTransform = false
  expr: Radius = data#<<data>>.WallThickness
FEATURE [PartDesign::CoordinateSystem] LCS_stepper_mount_1
  AttacherType = Attacher::AttachEngine3D
  MapMode = 11
  Placement = pos=(-13.35,70.5,25.4) rot=(0,0,1;1.5708rad)
  Support = -> [Fillet]
FEATURE [PartDesign::CoordinateSystem] LCS_gear02
  AttacherType = Attacher::AttachEngine3D
  MapMode = 11
  Placement = pos=(17.15,53,27.8) rot=(0,0,1;1.5708rad)
  Support = -> [Fillet]
FEATURE [PartDesign::CoordinateSystem] LCS_spacer
  AttacherType = Attacher::AttachEngine3D
  MapMode = 11
  Placement = pos=(17.15,53,35) rot=(0,0,1;1.5708rad)
  Support = -> [Fillet]
FEATURE [PartDesign::CoordinateSystem] LCS_pcb_1
  AttacherType = Attacher::AttachEngine3D
  MapMode = 11
  Placement = pos=(-23.15,-20.3,37) rot=(0,0,1;1.5708rad)
  Support = -> [Fillet]
FEATURE [PartDesign::CoordinateSystem] LCS_lcd
  AttacherType = Attacher::AttachEngine3D
  MapMode = 11
  Placement = pos=(15,-45,46.25) rot=(0,0,1;1.5708rad)
  Support = -> [Fillet]
FEATURE [PartDesign::CoordinateSystem] LCS_front
  AttacherType = Attacher::AttachEngine3D
  MapMode = 1
  Placement = pos=(-41.35,-19.55,38.6) rot=(0,0,1;3.14159rad)
  Support = -> [Fillet]
FEATURE [PartDesign::Body] Body_back
  Group = -> [LCS_0,Sketch,Pad,Sketch001,Pad001,Sketch002,Pad002,Sketch003,Pad003,Sketch004,Pad004,Sketch005,Pad005,Sketch006,Pad006,Sketch007,Pad007,Sketch008,Pad008,Fillet,LCS_stepper_mount_1,LCS_gear02,LCS_spacer,LCS_pcb_1,LCS_lcd,LCS_front]
  Origin = -> Origin
  Tip = -> Fillet
---- part Front.FCStd = doc fcstd_b4ad34a3bfb8 ----
FCSTD DOCUMENT  (FreeCAD 0.19R24291 (Git))
Label: Front
License: All rights reserved
LicenseURL: http://en.wikipedia.org/wiki/All_rights_reserved
objects: Sketcher::SketchObject×3, PartDesign::Pad×3, PartDesign::CoordinateSystem×2, PartDesign::Chamfer×1, Part::Part2DObjectPython×1, PartDesign::Pocket×1, PartDesign::Body×1
note: 17 computed .brp shape members not serialized (recipe doc carries the construction recipe); baked Part::Feature solids carry a one-line shape summary decoded from their .brp
EXTERNAL_REF file=data.FCStd obj=Spreadsheet

FEATURE [PartDesign::CoordinateSystem] LCS_0
  AttacherType = Attacher::AttachEngine3D
  MapMode = 2
  Support = -> [X_Axis]
FEATURE [Sketcher::SketchObject] Sketch  label="Sketch_front"
  FullyConstrained = true
  MapMode = 5
  Support = -> [XY_Plane]
  expr: Constraints[26] = data#<<data>>.OutsideWidth
  expr: Constraints[57] = data#<<data>>.WallThickness + data#<<data>>.LCDMountOffsetY
  expr: Constraints[10] = data#<<data>>.OutsideCornerRadius
  expr: Constraints[56] = data#<<data>>.LCDMountOffset
  expr: Constraints[25] = data#<<data>>.OutsideLength
  expr: Constraints[50] = data#<<data>>.LCDMountInsideDiameter
  expr: Constraints[60] = data#<<data>>.LCDViewLength
  expr: Constraints[65] = data#<<data>>.KnobShaftOffsetY
  expr: Constraints[64] = data#<<data>>.KnobShaftOffsetX
  expr: Constraints[54] = data#<<data>>.LCDWidth
  expr: Constraints[11] = data#<<data>>.OutsideRadius
  expr: Constraints[63] = data#<<data>>.KnobHoleDiameter
  expr: Constraints[53] = data#<<data>>.LCDLength
  expr: Constraints[55] = data#<<data>>.LCDMountOffset
  expr: Constraints[59] = data#<<data>>.LCDViewWidth
  expr: Constraints[58] = data#<<data>>.WallThickness + data#<<data>>.LCDMountOffsetX
  sketch-geometry (22):
    g0: ArcOfCircle CenterX=-37.75 CenterY=73.6 CenterZ=0 NormalX=0 NormalY=0 NormalZ=1 AngleXU=0 Radius=4.8 StartAngle=1.5708 EndAngle=3.14159
    g1: ArcOfCircle CenterX=17.15 CenterY=53 CenterZ=0 NormalX=0 NormalY=0 NormalZ=1 AngleXU=0 Radius=25.4 StartAngle=0 EndAngle=1.5708
    g2: ArcOfCircle CenterX=37.75 CenterY=-73.6 CenterZ=0 NormalX=0 NormalY=0 NormalZ=1 AngleXU=0 Radius=4.8 StartAngle=4.71239 EndAngle=6.28319
    g3: ArcOfCircle CenterX=-37.75 CenterY=-73.6 CenterZ=0 NormalX=0 NormalY=0 NormalZ=1 AngleXU=0 Radius=4.8 StartAngle=3.14159 EndAngle=4.71239
    g4: LineSegment StartX=-42.55 StartY=73.6 StartZ=0 EndX=-42.55 EndY=-73.6 EndZ=0
    g5: LineSegment StartX=-37.75 StartY=-78.4 StartZ=0 EndX=37.75 EndY=-78.4 EndZ=0
    g6: LineSegment StartX=42.55 StartY=-73.6 StartZ=0 EndX=42.55 EndY=53 EndZ=0
    g7: LineSegment StartX=17.15 StartY=78.4 StartZ=0 EndX=-37.75 EndY=78.4 EndZ=0
    g8: LineSegment StartX=-10.91 StartY=-51.14 StartZ=0 EndX=14 EndY=-51.14 EndZ=0
    g9: LineSegment StartX=14 StartY=-51.14 StartZ=0 EndX=14 EndY=-66 EndZ=0
    g10: LineSegment StartX=14 StartY=-66 StartZ=0 EndX=-10.91 EndY=-66 EndZ=0
    g11: LineSegment StartX=-10.91 StartY=-66 StartZ=0 EndX=-10.91 EndY=-51.14 EndZ=0
    g12: LineSegment StartX=-20 StartY=-40 StartZ=0 EndX=15 EndY=-40 EndZ=0
    g13: LineSegment StartX=15 StartY=-40 StartZ=0 EndX=15 EndY=-72 EndZ=0
    g14: LineSegment StartX=15 StartY=-72 StartZ=0 EndX=-20 EndY=-72 EndZ=0
    g15: LineSegment StartX=-20 StartY=-72 StartZ=0 EndX=-20 EndY=-40 EndZ=0
    g16: Circle CenterX=-17.5 CenterY=-42.5 CenterZ=0 NormalX=0 NormalY=0 NormalZ=1 AngleXU=0 Radius=1.4
    g17: Circle CenterX=12.5 CenterY=-42.5 CenterZ=0 NormalX=0 NormalY=0 NormalZ=1 AngleXU=0 Radius=1.4
    g18: Circle CenterX=12.5 CenterY=-69.5 CenterZ=0 NormalX=0 NormalY=0 NormalZ=1 AngleXU=0 Radius=1.4
    g19: Circle CenterX=-17.5 CenterY=-69.5 CenterZ=0 NormalX=0 NormalY=0 NormalZ=1 AngleXU=0 Radius=1.4
    g20: GeomPoint X=-2.5 Y=-56 Z=0
    g21: Circle CenterX=-7.55 CenterY=2.4 CenterZ=0 NormalX=0 NormalY=0 NormalZ=1 AngleXU=0 Radius=5.5
  constraints (66):
    c: Vertical(g0,g0)
    c: Vertical(g3,g3)
    c: Vertical(g2,g2)
    c: Vertical(g1,g1)
    c: Horizontal(g0,g0)
    c: Horizontal(g1,g1)
    c: Horizontal(g2,g2)
    c: Horizontal(g3,g3)
    c: Equal(g0,g3)
    c: Equal(g3,g2)
    c: Radius(g2) = 4.8
    c: Radius(g1) = 25.4
    c: Vertical(g1,g2)
    c: Vertical(g0,g3)
    c: Horizontal(g0,g1)
    c: Horizontal(g2,g3)
    c: Symmetric(g0,g2,g-1)
    c: Coincident(g4,g0)
    c: Coincident(g4,g3)
    c: Coincident(g5,g3)
    c: Coincident(g5,g2)
    c: Coincident(g6,g2)
    c: Coincident(g6,g1)
    c: Coincident(g7,g1)
    c: Coincident(g7,g0)
    c: DistanceY(g3,g0) = 156.8
    c: DistanceX(g3,g2) = 85.1
    c: Coincident(g8,g9)
    c: Coincident(g9,g10)
    c: Coincident(g10,g11)
    c: Coincident(g11,g8)
    c: Horizontal(g8)
    c: Horizontal(g10)
    c: Vertical(g9)
    c: Vertical(g11)
    c: Coincident(g12,g13)
    c: Coincident(g13,g14)
    c: Coincident(g14,g15)
    c: Coincident(g15,g12)
    c: Horizontal(g12)
    c: Horizontal(g14)
    c: Vertical(g13)
    c: Vertical(g15)
    c: Equal(g16,g17)
    c: Equal(g17,g18)
    c: Equal(g18,g19)
    c: Vertical(g16,g19)
    c: Vertical(g17,g18)
    c: Horizontal(g19,g18)
    c: Horizontal(g16,g17)
    c: Diameter(g17) = 2.8
    c: Symmetric(g12,g13,g20)
    c: Symmetric(g19,g17,g20)
    c: DistanceY(g15,g15) = 32
    c: DistanceX(g12,g12) = 35
    c: DistanceY(g16,g12) = 2.5
    c: DistanceX(g12,g16) = 2.5
    c: DistanceY(g2,g13) = 6.4
    c: DistanceX(g13,g2) = 27.55
    c: DistanceX(g8,g8) = 24.91
    c: DistanceY(g11,g11) = 14.86
    c: DistanceX(g9,g13) = 1
    c: DistanceY(g13,g9) = 6
    c: Diameter(g21) = 11
    c: DistanceX(g0,g21) = 35
    c: DistanceY(g21,g1) = 76
FEATURE [PartDesign::Pad] Pad
  Direction = (1,1,1)
  Length = 2.4
  Length2 = 100
  Profile = -> Sketch
  Type = 0
  expr: Length = data#<<data>>.WallThickness
FEATURE [Sketcher::SketchObject] Sketch001
  FullyConstrained = true
  MapMode = 5
  Support = -> [XY_Plane]
  expr: Constraints[73] = data#<<data>>.PCBLength
  expr: Constraints[75] = data#<<data>>.PCBGear02Y
  expr: Constraints[47] = data#<<data>>.OutsideLength
  expr: Constraints[63] = data#<<data>>.PowerJackWidth
  expr: Constraints[74] = data#<<data>>.PCBGear02X
  expr: Constraints[76] = data#<<data>>.PCBPowerJackY
  expr: Constraints[72] = data#<<data>>.PCBWidth
  expr: Constraints[34] = data#<<data>>.OutsideRadius
  expr: Constraints[33] = data#<<data>>.OutsideCornerRadius
  expr: Constraints[16] = data#<<data>>.MiddleRadius
  expr: Constraints[48] = data#<<data>>.OutsideWidth
  expr: Constraints[15] = data#<<data>>.MiddleCornerRadius
  sketch-geometry (24):
    g0: ArcOfCircle CenterX=-37.75 CenterY=73.6 CenterZ=0 NormalX=0 NormalY=0 NormalZ=1 AngleXU=0 Radius=3.6 StartAngle=1.5708 EndAngle=3.14159
    g1: ArcOfCircle CenterX=17.15 CenterY=53 CenterZ=0 NormalX=0 NormalY=0 NormalZ=1 AngleXU=0 Radius=24.2 StartAngle=0 EndAngle=1.5708
    g2: ArcOfCircle CenterX=37.75 CenterY=-73.6 CenterZ=0 NormalX=0 NormalY=0 NormalZ=1 AngleXU=0 Radius=3.6 StartAngle=4.71239 EndAngle=6.28319
    g3: ArcOfCircle CenterX=-37.75 CenterY=-73.6 CenterZ=0 NormalX=0 NormalY=0 NormalZ=1 AngleXU=0 Radius=3.6 StartAngle=3.14159 EndAngle=4.71239
    g4: LineSegment StartX=-37.75 StartY=77.2 StartZ=0 EndX=17.15 EndY=77.2 EndZ=0
    g5: LineSegment StartX=41.35 StartY=53 StartZ=0 EndX=41.35 EndY=-73.6 EndZ=0
    g6: LineSegment StartX=37.75 StartY=-77.2 StartZ=0 EndX=-37.75 EndY=-77.2 EndZ=0
    g7: ArcOfCircle CenterX=-37.75 CenterY=73.6 CenterZ=0 NormalX=0 NormalY=0 NormalZ=1 AngleXU=0 Radius=4.8 StartAngle=1.5708 EndAngle=3.14159
    g8: ArcOfCircle CenterX=17.15 CenterY=53 CenterZ=0 NormalX=0 NormalY=0 NormalZ=1 AngleXU=0 Radius=25.4 StartAngle=0 EndAngle=1.5708
    g9: ArcOfCircle CenterX=37.75 CenterY=-73.6 CenterZ=0 NormalX=0 NormalY=0 NormalZ=1 AngleXU=0 Radius=4.8 StartAngle=4.71239 EndAngle=6.28319
    g10: ArcOfCircle CenterX=-37.75 CenterY=-73.6 CenterZ=0 NormalX=0 NormalY=0 NormalZ=1 AngleXU=0 Radius=4.8 StartAngle=3.14159 EndAngle=4.71239
    g11: LineSegment StartX=-37.75 StartY=-78.4 StartZ=0 EndX=37.75 EndY=-78.4 EndZ=0
    g12: LineSegment StartX=42.55 StartY=53 StartZ=0 EndX=42.55 EndY=-73.6 EndZ=0
    g13: LineSegment StartX=17.15 StartY=78.4 StartZ=0 EndX=-37.75 EndY=78.4 EndZ=0
    g14: LineSegment StartX=-42.55 StartY=73.6 StartZ=0 EndX=-42.55 EndY=-10.05 EndZ=0
    g15: LineSegment StartX=-41.35 StartY=73.6 StartZ=0 EndX=-41.35 EndY=-10.05 EndZ=0
    g16: LineSegment StartX=-42.55 StartY=-73.6 StartZ=0 EndX=-42.55 EndY=-19.55 EndZ=0
    g17: LineSegment StartX=-41.35 StartY=-73.6 StartZ=0 EndX=-41.35 EndY=-19.55 EndZ=0
    g18: LineSegment StartX=-42.55 StartY=-10.05 StartZ=0 EndX=-41.35 EndY=-10.05 EndZ=0
    g19: LineSegment StartX=-42.55 StartY=-19.55 StartZ=0 EndX=-41.35 EndY=-19.55 EndZ=0
    g20: LineSegment StartX=-39.15 StartY=74.7 StartZ=0 EndX=20.85 EndY=74.7 EndZ=0
    g21: LineSegment StartX=20.85 StartY=74.7 StartZ=0 EndX=20.85 EndY=-25.3 EndZ=0
    g22: LineSegment StartX=20.85 StartY=-25.3 StartZ=0 EndX=-39.15 EndY=-25.3 EndZ=0
    g23: LineSegment StartX=-39.15 StartY=-25.3 StartZ=0 EndX=-39.15 EndY=74.7 EndZ=0
  constraints (77):
    c: Vertical(g0,g0)
    c: Vertical(g3,g3)
    c: Vertical(g1,g1)
    c: Vertical(g2,g2)
    c: Horizontal(g0,g0)
    c: Horizontal(g1,g1)
    c: Horizontal(g2,g2)
    c: Horizontal(g3,g3)
    c: Vertical(g0,g3)
    c: Vertical(g1,g2)
    c: Horizontal(g0,g1)
    c: Horizontal(g3,g2)
    c: Equal(g0,g3)
    c: Equal(g3,g2)
    c: Symmetric(g0,g2,g-1)
    c: Radius(g2) = 3.6
    c: Radius(g1) = 24.2
    c: Coincident(g4,g0)
    c: Coincident(g4,g1)
    c: Coincident(g5,g1)
    c: Coincident(g5,g2)
    c: Coincident(g6,g2)
    c: Coincident(g6,g3)
    c: Vertical(g7,g7)
    c: Vertical(g10,g10)
    c: Vertical(g9,g9)
    c: Vertical(g8,g8)
    c: Horizontal(g7,g7)
    c: Horizontal(g8,g8)
    c: Horizontal(g9,g9)
    c: Horizontal(g10,g10)
    c: Equal(g7,g10)
    c: Equal(g10,g9)
    c: Radius(g10) = 4.8
    c: Radius(g8) = 25.4
    c: Vertical(g7,g10)
    c: Vertical(g9,g8)
    c: Horizontal(g7,g8)
    c: Horizontal(g9,g10)
    c: Coincident(g7,g0)
    c: Coincident(g9,g2)
    c: Coincident(g11,g10)
    c: Coincident(g11,g9)
    c: Coincident(g12,g8)
    c: Coincident(g12,g9)
    c: Coincident(g13,g8)
    c: Coincident(g13,g7)
    c: DistanceY(g10,g7) = 156.8
    c: DistanceX(g7,g8) = 85.1
    c: Coincident(g14,g7)
    c: Vertical(g14)
    c: Coincident(g15,g0)
    c: Vertical(g15)
    c: Coincident(g16,g10)
    c: Vertical(g16)
    c: Coincident(g17,g3)
    c: Vertical(g17)
    c: Horizontal(g15,g14)
    c: Horizontal(g16,g17)
    c: Coincident(g18,g14)
    c: Coincident(g18,g15)
    c: Coincident(g19,g16)
    c: Coincident(g19,g17)
    c: DistanceY(g16,g14) = 9.5
    c: Coincident(g20,g21)
    c: Coincident(g21,g22)
    c: Coincident(g22,g23)
    c: Coincident(g23,g20)
    c: Horizontal(g20)
    c: Horizontal(g22)
    c: Vertical(g21)
    c: Vertical(g23)
    c: DistanceX(g20,g20) = 60
    c: DistanceY(g21,g21) = 100
    c: DistanceX(g1,g20) = 3.7
    c: DistanceY(g1,g20) = 21.7
    c: DistanceY(g22,g16) = 5.75
FEATURE [PartDesign::Pad] Pad001
  BaseFeature = -> Pad
  Direction = (1,1,1)
  Length = 11
  Length2 = 100
  Profile = -> Sketch001
  Reversed = true
  Type = 0
  expr: Length = data#<<data>>.Wall3Height
FEATURE [PartDesign::Chamfer] Chamfer
  Angle = 42
  Base = -> Pad001 [Edge22,Edge21,Edge24,Edge23]
  BaseFeature = -> Pad001
  ChamferType = 0
  FlipDirection = false
  Size = 2
  Size2 = 2
  SupportTransform = false
FEATURE [Sketcher::SketchObject] Sketch002
  FullyConstrained = true
  MapMode = 5
  Support = -> [XY_Plane]
  expr: Constraints[22] = data#<<data>>.InsideRadius
  expr: Constraints[7] = data#<<data>>.OutsideLength
  expr: Constraints[13] = data#<<data>>.OutsideLowAngle
  expr: Constraints[10] = data#<<data>>.OutsideRadius
  expr: Constraints[8] = data#<<data>>.OutsideWidth
  sketch-geometry (14):
    g0: LineSegment StartX=-42.55 StartY=78.4 StartZ=0 EndX=-42.55 EndY=-78.4 EndZ=0
    g1: LineSegment StartX=-42.55 StartY=-78.4 StartZ=0 EndX=42.55 EndY=-78.4 EndZ=0
    g2: LineSegment StartX=-42.55 StartY=78.4 StartZ=0 EndX=17.15 EndY=78.4 EndZ=0
    g3: ArcOfCircle CenterX=17.15 CenterY=53 CenterZ=0 NormalX=0 NormalY=0 NormalZ=1 AngleXU=0 Radius=25.4 StartAngle=0 EndAngle=1.55505
    g4: LineSegment StartX=17.15 StartY=53 StartZ=0 EndX=42.55 EndY=31.6869 EndZ=0
    g5: LineSegment StartX=42.55 StartY=53 StartZ=0 EndX=42.55 EndY=32.0869 EndZ=0
    g6: LineSegment StartX=-40.15 StartY=76 StartZ=0 EndX=17.15 EndY=76 EndZ=0
    g7: LineSegment StartX=-40.15 StartY=76 StartZ=0 EndX=-40.15 EndY=-76 EndZ=0
    g8: LineSegment StartX=-40.15 StartY=-76 StartZ=0 EndX=40.15 EndY=-76 EndZ=0
    g9: ArcOfCircle CenterX=17.15 CenterY=53 CenterZ=0 NormalX=0 NormalY=0 NormalZ=1 AngleXU=0 Radius=23 StartAngle=0 EndAngle=1.5534
    g10: LineSegment StartX=40.15 StartY=53 StartZ=0 EndX=40.15 EndY=32.0869 EndZ=0
    g11: LineSegment StartX=40.15 StartY=31.6869 StartZ=0 EndX=42.55 EndY=31.6869 EndZ=0
    g12: LineSegment StartX=17.55 StartY=78.3969 StartZ=0 EndX=17.55 EndY=75.9965 EndZ=0
    g13: LineSegment StartX=40.15 StartY=32.0869 StartZ=0 EndX=42.55 EndY=32.0869 EndZ=0
  constraints (43):
    c: Vertical(g0)
    c: Coincident(g1,g0)
    c: Horizontal(g1)
    c: Coincident(g2,g0)
    c: Horizontal(g2)
    c: Horizontal(g3,g3)
    c: Vertical(g3,g1)
    c: DistanceY(g0,g0) = 156.8
    c: DistanceX(g1,g1) = 85.1
    c: Symmetric(g0,g1,g-1)
    c: Radius(g3) = 25.4
    c: Coincident(g4,g3)
    c: Vertical(g3,g4)
    c: Angle(g-2,g4) = 0.872665
    c: Coincident(g5,g3)
    c: Horizontal(g6)
    c: Coincident(g7,g6)
    c: Vertical(g7)
    c: Coincident(g8,g7)
    c: Horizontal(g8)
    c: Symmetric(g6,g8,g-1)
    c: Horizontal(g9,g9)
    c: Radius(g9) = 23
    c: Coincident(g9,g3)
    c: Vertical(g9,g8)
    c: Coincident(g10,g9)
    c: Coincident(g11,g4)
    c: Vertical(g10)
    c: Vertical(g12)
    c: DistanceX(g2,g12) = 0.4
    c: Coincident(g3,g12)
    c: Coincident(g9,g12)
    c: PointOnObject(g2,g3)
    c: PointOnObject(g6,g9)
    c: Vertical(g3,g6)
    c: Vertical(g6,g2)
    c: Horizontal(g13)
    c: DistanceY(g4,g13) = 0.4
    c: Coincident(g10,g13)
    c: Coincident(g5,g13)
    c: Vertical(g5,g4)
    c: Vertical(g10,g11)
    c: Horizontal(g11)
FEATURE [PartDesign::Pad] Pad002
  BaseFeature = -> Chamfer
  Direction = (1,1,1)
  Length = 14.6
  Length2 = 100
  Profile = -> Sketch002
  Reversed = true
  Type = 0
  expr: Length = data#<<data>>.Wall3Height + data#<<data>>.PCBThickness + data#<<data>>.HallSensorGap
FEATURE [Part::Part2DObjectPython] ShapeString  # Draft 2D object (typed FeaturePython)
  FontFile = /System/Library/Fonts/Supplemental/Georgia Bold.ttf
  Placement = pos=(-38,30,2.4) rot=(0,0,1;0rad)
  Size = 30
  String = Tea
  Tracking = 0
  expr: .Placement.Base.z = data#<<data>>.WallThickness
FEATURE [PartDesign::Pocket] Pocket
  BaseFeature = -> Pad002
  Length = 0.4
  Length2 = 100
  Profile = -> ShapeString
  Type = 0
FEATURE [PartDesign::CoordinateSystem] LCS_back
  AttacherType = Attacher::AttachEngine3D
  MapMode = 1
  Placement = pos=(-41.35,-19.55,-11) rot=(0,0,1;0rad)
  Support = -> [Pocket]
FEATURE [PartDesign::Body] Body_front
  Group = -> [LCS_0,Sketch,Pad,Sketch001,Pad001,Chamfer,LCS_back,Sketch002,Pad002,ShapeString,Pocket]
  Origin = -> Origin
  Tip = -> Pocket
---- part Gear01.FCStd = doc fcstd_703fe51fd5ed ----
FCSTD DOCUMENT  (FreeCAD 0.19R24291 (Git))
Label: Gear01
License: All rights reserved
LicenseURL: http://en.wikipedia.org/wiki/All_rights_reserved
objects: Sketcher::SketchObject×2, PartDesign::Pocket×2, PartDesign::CoordinateSystem×1, PartDesign::FeaturePython×1, PartDesign::Body×1, App::Part×1
note: 9 computed .brp shape members not serialized (recipe doc carries the construction recipe); baked Part::Feature solids carry a one-line shape summary decoded from their .brp
EXTERNAL_REF file=data.FCStd obj=Spreadsheet

FEATURE [PartDesign::CoordinateSystem] LCS_0
  AttacherType = Attacher::AttachEngine3D
  AttachmentOffset = pos=(0,0,2.5) rot=(0,0,1;0rad)
  MapMode = 2
  Placement = pos=(0,0,2.5) rot=(0,0,1;0rad)
  Support = -> [X_Axis]
FEATURE [PartDesign::FeaturePython] involutegear  # WARN: FeaturePython — macro-defined, semantics opaque (R4)
  AttacherType = Attacher::AttachEngine3D
  backlash = 0
  beta = 0
  clearance = 0.25
  da = 17
  df = 12.5
  double_helix = false
  dw = 15
  head = 0
  height = 8.5
  module = 1
  numpoints = 6
  pressure_angle = 20
  properties_from_tool = false
  reversed_backlash = false
  shift = 0
  simple = false
  teeth = 15
  transverse_pitch = 3.14159
  undercut = false
  version = 0.0.3
  expr: teeth = data#<<data>>.Gear01Teeth
  expr: module = data#<<data>>.GearModule
  expr: height = data#<<data>>.Gear01Thickness
FEATURE [Sketcher::SketchObject] Sketch
  FullyConstrained = true
  MapMode = 5
  Support = -> [XY_Plane001]
  expr: Constraints[0] = data#<<data>>.StepperShaftDiameter
  sketch-geometry (1):
    g0: Circle CenterX=0 CenterY=0 CenterZ=0 NormalX=0 NormalY=0 NormalZ=1 AngleXU=0 Radius=2.6
  constraints (2):
    c: Diameter(g0) = 5.2
    c: Coincident(g0,g-1)
FEATURE [PartDesign::Pocket] Pocket
  BaseFeature = -> involutegear
  Length = 2.5
  Length2 = 100
  Profile = -> Sketch
  Reversed = true
  Type = 0
FEATURE [Sketcher::SketchObject] Sketch001
  FullyConstrained = true
  MapMode = 5
  Support = -> [XY_Plane001]
  expr: Constraints[11] = data#<<data>>.StepperShaftRectWidth
  expr: Constraints[10] = data#<<data>>.StepperShaftDiameter
  sketch-geometry (4):
    g0: ArcOfCircle CenterX=0 CenterY=0 CenterZ=0 NormalX=0 NormalY=0 NormalZ=1 AngleXU=0 Radius=2.6 StartAngle=0.907923 EndAngle=2.23367
    g1: LineSegment StartX=-1.6 StartY=2.04939 StartZ=0 EndX=-1.6 EndY=-2.04939 EndZ=0
    g2: LineSegment StartX=1.6 StartY=2.04939 StartZ=0 EndX=1.6 EndY=-2.04939 EndZ=0
    g3: ArcOfCircle CenterX=0 CenterY=0 CenterZ=0 NormalX=0 NormalY=0 NormalZ=1 AngleXU=0 Radius=2.6 StartAngle=4.04952 EndAngle=5.37526
  constraints (12):
    c: Coincident(g0,g-1)
    c: Vertical(g1)
    c: Vertical(g2)
    c: Symmetric(g1,g2,g-2)
    c: Coincident(g0,g2)
    c: Coincident(g3,g2)
    c: Equal(g0,g3)
    c: PointOnObject(g0,g1)
    c: Coincident(g3,g1)
    c: Coincident(g0,g3)
    c: Diameter(g0) = 5.2
    c: DistanceX(g0,g0) = 3.2
FEATURE [PartDesign::Pocket] Pocket001
  BaseFeature = -> Pocket
  Length = 5
  Length2 = 100
  Profile = -> Sketch001
  Reversed = true
  Type = 1
FEATURE [PartDesign::Body] Body  label="Body_gear01"
  Group = -> [involutegear,Sketch,Pocket,Sketch001,Pocket001]
  Origin = -> Origin001
  Tip = -> Pocket001
FEATURE [App::Part] Part_gear01
  Group = -> [LCS_0,Body]
  Origin = -> Origin
---- part Gear02.FCStd = doc fcstd_434fd255d060 ----
FCSTD DOCUMENT  (FreeCAD 0.19R24291 (Git))
Label: Gear02
License: All rights reserved
LicenseURL: http://en.wikipedia.org/wiki/All_rights_reserved
objects: Sketcher::SketchObject×4, PartDesign::Pocket×3, PartDesign::CoordinateSystem×1, PartDesign::FeaturePython×1, PartDesign::Pad×1, PartDesign::Body×1, App::Part×1
note: 15 computed .brp shape members not serialized (recipe doc carries the construction recipe); baked Part::Feature solids carry a one-line shape summary decoded from their .brp
EXTERNAL_REF file=data.FCStd obj=Spreadsheet

FEATURE [PartDesign::CoordinateSystem] LCS_0
  AttacherType = Attacher::AttachEngine3D
  MapMode = 2
  Support = -> [X_Axis]
FEATURE [PartDesign::FeaturePython] involutegear  # WARN: FeaturePython — macro-defined, semantics opaque (R4)
  AttacherType = Attacher::AttachEngine3D
  backlash = 0
  beta = 0
  clearance = 0.25
  da = 32
  df = 27.5
  double_helix = false
  dw = 30
  head = 0
  height = 7
  module = 1
  numpoints = 6
  pressure_angle = 20
  properties_from_tool = false
  reversed_backlash = false
  shift = 0
  simple = false
  teeth = 30
  transverse_pitch = 3.14159
  undercut = false
  version = 0.0.3
  expr: teeth = data#<<data>>.Gear02Teeth
  expr: module = data#<<data>>.GearModule
  expr: height = data#<<data>>.Gear02Thickness
FEATURE [Sketcher::SketchObject] Sketch
  FullyConstrained = true
  MapMode = 5
  Support = -> [XY_Plane001]
  expr: Constraints[1] = data#<<data>>.Gear02ShaftHole
  sketch-geometry (1):
    g0: Circle CenterX=0 CenterY=0 CenterZ=0 NormalX=0 NormalY=0 NormalZ=1 AngleXU=0 Radius=3
  constraints (2):
    c: Coincident(g0,g-1)
    c: Diameter(g0) = 6
FEATURE [PartDesign::Pocket] Pocket
  BaseFeature = -> involutegear
  Length = 5
  Length2 = 100
  Profile = -> Sketch
  Reversed = true
  Type = 1
FEATURE [Sketcher::SketchObject] Sketch001
  FullyConstrained = true
  MapMode = 5
  Support = -> [XY_Plane001]
  expr: Constraints[32] = data#<<data>>.Gear02NotchOffset
  expr: Constraints[27] = data#<<data>>.Gear02NotchCornerRadius
  expr: Constraints[30] = data#<<data>>.Gear02LeverWidth
  expr: Constraints[10] = data#<<data>>.Gear02LeverLength
  expr: Constraints[9] = data#<<data>>.Gear02LeverOffset
  sketch-geometry (12):
    g0: LineSegment StartX=5 StartY=84 StartZ=0 EndX=5 EndY=4 EndZ=0
    g1: LineSegment StartX=5 StartY=4 StartZ=0 EndX=-5 EndY=4 EndZ=0
    g2: LineSegment StartX=-5 StartY=4 StartZ=0 EndX=-5 EndY=77.6 EndZ=0
    g3: ArcOfCircle CenterX=0 CenterY=84 CenterZ=0 NormalX=0 NormalY=0 NormalZ=1 AngleXU=0 Radius=5 StartAngle=4.11372e-06 EndAngle=3.14159
    g4: LineSegment StartX=-3.8 StartY=81.8 StartZ=0 EndX=-1.2 EndY=81.8 EndZ=0
    g5: LineSegment StartX=0 StartY=80.6 StartZ=0 EndX=0 EndY=80 EndZ=0
    g6: LineSegment StartX=-1.2 StartY=78.8 StartZ=0 EndX=-3.8 EndY=78.8 EndZ=0
    g7: LineSegment StartX=-5 StartY=83 StartZ=0 EndX=-5 EndY=84 EndZ=0
    g8: ArcOfCircle CenterX=-3.8 CenterY=83 CenterZ=0 NormalX=0 NormalY=0 NormalZ=1 AngleXU=0 Radius=1.2 StartAngle=3.14159 EndAngle=4.71239
    g9: ArcOfCircle CenterX=-1.2 CenterY=80.6 CenterZ=0 NormalX=0 NormalY=0 NormalZ=1 AngleXU=0 Radius=1.2 StartAngle=3.8e-15 EndAngle=1.5708
    g10: ArcOfCircle CenterX=-1.2 CenterY=80 CenterZ=0 NormalX=0 NormalY=0 NormalZ=1 AngleXU=0 Radius=1.2 StartAngle=4.71239 EndAngle=6.28319
    g11: ArcOfCircle CenterX=-3.8 CenterY=77.6 CenterZ=0 NormalX=0 NormalY=0 NormalZ=1 AngleXU=0 Radius=1.2 StartAngle=1.5708 EndAngle=3.14159
  constraints (33):
    c: Coincident(g0,g1)
    c: Coincident(g1,g2)
    c: Horizontal(g1)
    c: Vertical(g0)
    c: Vertical(g2)
    c: PointOnObject(g3,g-2)
    c: Coincident(g3,g7)
    c: Coincident(g3,g0)
    c: Horizontal(g7,g3)
    c: DistanceY(g-1,g0) = 4
    c: DistanceY(g0,g0) = 80
    c: Radius(g3) = 5
    c: Horizontal(g4)
    c: Vertical(g5)
    c: Horizontal(g6)
    c: Tangent(g2,g7)
    c: Tangent(g7,g8) = 1.5708
    c: Tangent(g4,g8) = -1.5708
    c: Tangent(g4,g9) = 1.5708
    c: Tangent(g5,g9) = 1.5708
    c: Tangent(g5,g10) = 1.5708
    c: Tangent(g6,g10) = 1.5708
    c: Tangent(g6,g11) = -1.5708
    c: Tangent(g2,g11) = 1.5708
    c: Equal(g8,g9)
    c: Equal(g9,g10)
    c: Equal(g10,g11)
    c: Radius(g8) = 1.2
    c: DistanceY(g6,g4) = 3
    c: PointOnObject(g5,g-2)
    c: DistanceX(g3,g0) = 10
    c: DistanceY(g-1,g4) = 81.8  'channel_start'
    c: DistanceY(g7,g3) = 1
FEATURE [PartDesign::Pad] Pad
  BaseFeature = -> Pocket
  Direction = (1,1,1)
  Length = 7
  Length2 = 100
  Profile = -> Sketch001
  Type = 0
  expr: Length = data#<<data>>.Gear02Thickness
FEATURE [Sketcher::SketchObject] Sketch002
  AttachmentOffset = pos=(0,0,7) rot=(0,0,1;0rad)
  FullyConstrained = true
  MapMode = 5
  Placement = pos=(0,0,7) rot=(0,0,1;0rad)
  Support = -> [XY_Plane001]
  expr: Constraints[5] = data#<<data>>.MagnetDistanceOnGear
  expr: Constraints[0] = data#<<data>>.MagnetDiameter
  expr: .AttachmentOffset.Base.z = data#<<data>>.Gear02Thickness
  expr: Constraints[7] = data#<<data>>.MagnetAngle
  sketch-geometry (3):
    g0: Circle CenterX=-10.5 CenterY=1.5e-15 CenterZ=0 NormalX=0 NormalY=0 NormalZ=1 AngleXU=0 Radius=2.5
    g1: LineSegment StartX=0 StartY=0 StartZ=0 EndX=-10.5 EndY=1.5e-15 EndZ=0
    g2: LineSegment StartX=0 StartY=0 StartZ=0 EndX=0 EndY=-10.5 EndZ=0
  constraints (8):
    c: Diameter(g0) = 5
    c: Coincident(g1,g-1)
    c: Coincident(g2,g-1)
    c: PointOnObject(g2,g-2)
    c: Equal(g1,g2)
    c: Distance(g1) = 10.5
    c: Coincident(g0,g1)
    c: Angle(g-2,g1) = 1.5708
FEATURE [PartDesign::Pocket] Pocket001
  BaseFeature = -> Pad
  Length = 3
  Length2 = 100
  Profile = -> Sketch002
  Type = 0
  expr: Length = data#<<data>>.MagnetThickness
FEATURE [Sketcher::SketchObject] Sketch003
  AttachmentOffset = pos=(0,0,-81.8) rot=(0,0,1;0rad)
  FullyConstrained = true
  MapMode = 5
  Placement = pos=(0,81.8,1.82e-14) rot=(1,0,0;1.5708rad)
  Support = -> [XZ_Plane001]
  expr: .AttachmentOffset.Base.z = -data#<<data>>.Gear02SlotStart
  expr: Constraints[3] = data#<<data>>.Gear02SlotDiameter
  expr: Constraints[4] = data#<<data>>.Gear02LeverWidth / 2
  expr: Constraints[2] = data#<<data>>.Gear02Thickness / 2
  sketch-geometry (2):
    g0: ArcOfCircle CenterX=-5 CenterY=3.5 CenterZ=0 NormalX=0 NormalY=0 NormalZ=1 AngleXU=0 Radius=1.16667 StartAngle=4.71239 EndAngle=7.85398
    g1: LineSegment StartX=-5 StartY=4.66667 StartZ=0 EndX=-5 EndY=2.33333 EndZ=0
  constraints (7):
    c: Vertical(g0,g0)
    c: Vertical(g0,g0)
    c: DistanceY(g-1,g0) = 3.5
    c: Diameter(g0) = 2.33333
    c: DistanceX(g1,g-1) = 5
    c: Coincident(g1,g0)
    c: Coincident(g1,g0)
FEATURE [PartDesign::Pocket] Pocket002
  BaseFeature = -> Pocket001
  Length = 11
  Length2 = 100
  Profile = -> Sketch003
  Type = 1
FEATURE [PartDesign::Body] Body  label="Body_gear02"
  Group = -> [involutegear,Sketch,Pocket,Sketch001,Pad,Sketch002,Pocket001,Sketch003,Pocket002]
  Origin = -> Origin001
  Tip = -> Pocket002
FEATURE [App::Part] Part_gear02
  Group = -> [LCS_0,Body]
  Origin = -> Origin
---- part Gear02Cap.FCStd = doc fcstd_f2f772aded51 ----
FCSTD DOCUMENT  (FreeCAD 0.19R24291 (Git))
Label: Gear02Cap
License: All rights reserved
LicenseURL: http://en.wikipedia.org/wiki/All_rights_reserved
objects: PartDesign::CoordinateSystem×2, Sketcher::SketchObject×1, PartDesign::Pad×1, PartDesign::Body×1
note: 6 computed .brp shape members not serialized (recipe doc carries the construction recipe); baked Part::Feature solids carry a one-line shape summary decoded from their .brp
EXTERNAL_REF file=data.FCStd obj=Spreadsheet

FEATURE [PartDesign::CoordinateSystem] LCS_0
  AttacherType = Attacher::AttachEngine3D
  MapMode = 2
  Support = -> [X_Axis]
FEATURE [Sketcher::SketchObject] Sketch
  FullyConstrained = true
  MapMode = 5
  Support = -> [XY_Plane]
  expr: Constraints[2] = data#<<data>>.M3DiameterHole
  expr: Constraints[3] = data#<<data>>.Gear02ShaftDiameter * 2
  sketch-geometry (2):
    g0: Circle CenterX=0 CenterY=0 CenterZ=0 NormalX=0 NormalY=0 NormalZ=1 AngleXU=0 Radius=6
    g1: Circle CenterX=0 CenterY=0 CenterZ=0 NormalX=0 NormalY=0 NormalZ=1 AngleXU=0 Radius=1.7
  constraints (4):
    c: Coincident(g0,g-1)
    c: Coincident(g1,g0)
    c: Diameter(g1) = 3.4
    c: Diameter(g0) = 12
FEATURE [PartDesign::Pad] Pad
  Direction = (1,1,1)
  Length = 2
  Length2 = 100
  Profile = -> Sketch
  Type = 0
  expr: Length = data#<<data>>.HallSensorGap
FEATURE [PartDesign::CoordinateSystem] LCS_pcb
  AttacherType = Attacher::AttachEngine3D
  MapMode = 11
  Placement = pos=(0,0,2) rot=(0,0,1;1.5708rad)
  Support = -> [Pad]
FEATURE [PartDesign::Body] Body_gear02cap
  Group = -> [LCS_0,Sketch,Pad,LCS_pcb]
  Origin = -> Origin
  Tip = -> Pad
---- part LCD114.FCStd = doc fcstd_50e289ac497f ----
FCSTD DOCUMENT  (FreeCAD 0.19R24291 (Git))
Label: LCD114
License: All rights reserved
LicenseURL: http://en.wikipedia.org/wiki/All_rights_reserved
objects: Sketcher::SketchObject×3, PartDesign::Pad×3, PartDesign::CoordinateSystem×2, PartDesign::Body×1
note: 12 computed .brp shape members not serialized (recipe doc carries the construction recipe); baked Part::Feature solids carry a one-line shape summary decoded from their .brp
EXTERNAL_REF file=data.FCStd obj=Spreadsheet

FEATURE [PartDesign::CoordinateSystem] LCS_0
  AttacherType = Attacher::AttachEngine3D
  MapMode = 2
  Support = -> [X_Axis]
FEATURE [Sketcher::SketchObject] Sketch  label="Sketch_PCB"
  FullyConstrained = true
  MapMode = 5
  Support = -> [XY_Plane]
  expr: Constraints[44] = data#<<data>>.LCDLength
  expr: Constraints[43] = data#<<data>>.LCDWidth
  expr: Constraints[42] = data#<<data>>.LCDMountOffset
  sketch-geometry (16):
    g0: ArcOfCircle CenterX=-15 CenterY=13.5 CenterZ=0 NormalX=0 NormalY=0 NormalZ=1 AngleXU=0 Radius=2.5 StartAngle=1.5708 EndAngle=3.14159
    g1: ArcOfCircle CenterX=15 CenterY=13.5 CenterZ=0 NormalX=0 NormalY=0 NormalZ=1 AngleXU=0 Radius=2.5 StartAngle=0 EndAngle=1.5708
    g2: ArcOfCircle CenterX=15 CenterY=-13.5 CenterZ=0 NormalX=0 NormalY=0 NormalZ=1 AngleXU=0 Radius=2.5 StartAngle=4.71239 EndAngle=6.28319
    g3: ArcOfCircle CenterX=-15 CenterY=-13.5 CenterZ=0 NormalX=0 NormalY=0 NormalZ=1 AngleXU=0 Radius=2.5 StartAngle=3.14159 EndAngle=4.71239
    g4: LineSegment StartX=-17.5 StartY=13.5 StartZ=0 EndX=-17.5 EndY=-13.5 EndZ=0
    g5: LineSegment StartX=17.5 StartY=13.5 StartZ=0 EndX=17.5 EndY=-13.5 EndZ=0
    g6: LineSegment StartX=-15 StartY=16 StartZ=0 EndX=15 EndY=16 EndZ=0
    g7: LineSegment StartX=-15 StartY=-16 StartZ=0 EndX=15 EndY=-16 EndZ=0
    g8: LineSegment StartX=-17.5 StartY=13.5 StartZ=0 EndX=-17.5 EndY=16 EndZ=0
    g9: LineSegment StartX=-15 StartY=16 StartZ=0 EndX=-17.5 EndY=16 EndZ=0
    g10: LineSegment StartX=17.5 StartY=-13.5 StartZ=0 EndX=17.5 EndY=-16 EndZ=0
    g11: LineSegment StartX=15 StartY=-16 StartZ=0 EndX=17.5 EndY=-16 EndZ=0
    g12: Circle CenterX=-15 CenterY=13.5 CenterZ=0 NormalX=0 NormalY=0 NormalZ=1 AngleXU=0 Radius=1.5
    g13: Circle CenterX=15 CenterY=13.5 CenterZ=0 NormalX=0 NormalY=0 NormalZ=1 AngleXU=0 Radius=1.5
    g14: Circle CenterX=15 CenterY=-13.5 CenterZ=0 NormalX=0 NormalY=0 NormalZ=1 AngleXU=0 Radius=1.5
    g15: Circle CenterX=-15 CenterY=-13.5 CenterZ=0 NormalX=0 NormalY=0 NormalZ=1 AngleXU=0 Radius=1.5
  constraints (45):
    c: Vertical(g0,g0)
    c: Vertical(g3,g3)
    c: Vertical(g1,g1)
    c: Vertical(g2,g2)
    c: Horizontal(g0,g0)
    c: Horizontal(g1,g1)
    c: Horizontal(g2,g2)
    c: Horizontal(g3,g3)
    c: Equal(g0,g1)
    c: Equal(g0,g2)
    c: Equal(g0,g3)
    c: Coincident(g4,g0)
    c: Coincident(g5,g1)
    c: Coincident(g6,g0)
    c: Coincident(g7,g3)
    c: Coincident(g8,g0)
    c: Vertical(g8)
    c: Coincident(g9,g0)
    c: Horizontal(g9)
    c: Coincident(g9,g8)
    c: Coincident(g10,g2)
    c: Vertical(g10)
    c: Coincident(g11,g2)
    c: Horizontal(g11)
    c: Coincident(g10,g11)
    c: Coincident(g4,g3)
    c: Coincident(g7,g2)
    c: Coincident(g6,g1)
    c: Coincident(g5,g2)
    c: Horizontal(g6)
    c: Horizontal(g7)
    c: Vertical(g4)
    c: Vertical(g5)
    c: Symmetric(g8,g10,g-1)
    c: Coincident(g12,g0)
    c: Coincident(g13,g1)
    c: Coincident(g14,g2)
    c: Coincident(g15,g3)
    c: Equal(g12,g13)
    c: Equal(g13,g14)
    c: Equal(g14,g15)
    c: Diameter(g12) = 3
    c: Radius(g1) = 2.5
    c: DistanceX(g3,g2) = 35
    c: DistanceY(g3,g0) = 32
FEATURE [PartDesign::Pad] Pad  label="Pad_PCB"
  Direction = (1,1,1)
  Length = 1.6
  Length2 = 100
  Profile = -> Sketch
  Type = 0
  expr: Length = data#<<data>>.LCDPCBThickness
FEATURE [Sketcher::SketchObject] Sketch001  label="Sketch_glass"
  AttachmentOffset = pos=(0,0,1.6) rot=(0,0,1;0rad)
  FullyConstrained = true
  MapMode = 5
  Placement = pos=(0,0,1.6) rot=(0,0,1;0rad)
  Support = -> [XY_Plane]
  expr: .AttachmentOffset.Base.z = data#<<data>>.LCDPCBThickness
  sketch-geometry (7):
    g0: LineSegment StartX=-15.5 StartY=7.5 StartZ=0 EndX=9.41 EndY=7.5 EndZ=0
    g1: LineSegment StartX=9.41 StartY=-7.5 StartZ=0 EndX=-15.5 EndY=-7.5 EndZ=0
    g2: LineSegment StartX=-15.5 StartY=-7.5 StartZ=0 EndX=-15.5 EndY=7.5 EndZ=0
    g3: LineSegment StartX=9.41 StartY=7.5 StartZ=0 EndX=15.5 EndY=7.5 EndZ=0
    g4: LineSegment StartX=15.5 StartY=7.5 StartZ=0 EndX=15.5 EndY=-7.5 EndZ=0
    g5: LineSegment StartX=15.5 StartY=-7.5 StartZ=0 EndX=9.41 EndY=-7.5 EndZ=0
    g6: LineSegment StartX=9.41 StartY=7.5 StartZ=0 EndX=9.41 EndY=-7.5 EndZ=0
  constraints (19):
    c: Coincident(g1,g2)
    c: Coincident(g2,g0)
    c: Horizontal(g0)
    c: Horizontal(g1)
    c: Vertical(g2)
    c: DistanceY(g2,g2) = 15
    c: DistanceX(g1,g1) = 24.91
    c: Coincident(g3,g4)
    c: Coincident(g4,g5)
    c: Horizontal(g3)
    c: Horizontal(g5)
    c: Vertical(g4)
    c: Coincident(g3,g0)
    c: DistanceX(g1,g4) = 31
    c: Symmetric(g0,g4,g-1)
    c: Coincident(g6,g0)
    c: Coincident(g6,g1)
    c: Vertical(g6)
    c: Coincident(g5,g1)
FEATURE [PartDesign::Pad] Pad001  label="Pad_glass"
  BaseFeature = -> Pad
  Direction = (1,1,1)
  Length = 1.75
  Length2 = 100
  Profile = -> Sketch001
  Type = 0
  expr: Length = data#<<data>>.LCDGlassThickness
FEATURE [Sketcher::SketchObject] Sketch002  label="Sketch_JST_PH_8"
  FullyConstrained = true
  MapMode = 5
  Support = -> [XY_Plane]
  sketch-geometry (9):
    g0: LineSegment StartX=-17.5 StartY=16 StartZ=0 EndX=17.5 EndY=16 EndZ=0
    g1: LineSegment StartX=17.5 StartY=16 StartZ=0 EndX=17.5 EndY=-16 EndZ=0
    g2: LineSegment StartX=17.5 StartY=-16 StartZ=0 EndX=-17.5 EndY=-16 EndZ=0
    g3: LineSegment StartX=-17.5 StartY=-16 StartZ=0 EndX=-17.5 EndY=16 EndZ=0
    g4: LineSegment StartX=-10 StartY=-8 StartZ=0 EndX=10 EndY=-8 EndZ=0
    g5: LineSegment StartX=10 StartY=-8 StartZ=0 EndX=10 EndY=-16 EndZ=0
    g6: LineSegment StartX=10 StartY=-16 StartZ=0 EndX=-10 EndY=-16 EndZ=0
    g7: LineSegment StartX=-10 StartY=-16 StartZ=0 EndX=-10 EndY=-8 EndZ=0
    g8: GeomPoint X=-1e-16 Y=-16 Z=0
  constraints (23):
    c: Coincident(g0,g1)
    c: Coincident(g1,g2)
    c: Coincident(g2,g3)
    c: Coincident(g3,g0)
    c: Horizontal(g0)
    c: Horizontal(g2)
    c: Vertical(g1)
    c: Vertical(g3)
    c: Symmetric(g0,g1,g-1)
    c: DistanceY(g3,g3) = 32
    c: DistanceX(g0,g0) = 35
    c: Coincident(g4,g5)
    c: Coincident(g5,g6)
    c: Coincident(g6,g7)
    c: Coincident(g7,g4)
    c: Horizontal(g4)
    c: Horizontal(g6)
    c: Vertical(g5)
    c: Vertical(g7)
    c: Symmetric(g2,g1,g8)
    c: DistanceX(g4,g4) = 20
    c: Symmetric(g6,g5,g8)
    c: DistanceY(g7,g7) = 8
FEATURE [PartDesign::Pad] Pad002
  BaseFeature = -> Pad001
  Direction = (1,1,1)
  Length = 5.5
  Length2 = 100
  Profile = -> Sketch002
  Reversed = true
  Type = 0
FEATURE [PartDesign::CoordinateSystem] LCS_mount
  AttacherType = Attacher::AttachEngine3D
  MapMode = 11
  Placement = pos=(-15,-13.5,0) rot=(0,0,1;1.5708rad)
  Support = -> [Pad002]
FEATURE [PartDesign::Body] Body_lcd1_14  label="Body_LCD114"
  Group = -> [LCS_0,Sketch,Pad,Sketch001,Pad001,Sketch002,Pad002,LCS_mount]
  Origin = -> Origin
  Tip = -> Pad002
---- part PCB.FCStd = doc fcstd_c50cb07c7492 ----
FCSTD DOCUMENT  (FreeCAD 0.19R24291 (Git))
Label: PCB
License: All rights reserved
LicenseURL: http://en.wikipedia.org/wiki/All_rights_reserved
objects: Part::Feature×13, App::Part×5, App::Link×5, PartDesign::CoordinateSystem×3, Sketcher::SketchObject×1
note: 17 computed .brp shape members not serialized (recipe doc carries the construction recipe); baked Part::Feature solids carry a one-line shape summary decoded from their .brp

FEATURE [PartDesign::CoordinateSystem] Local_CS_18fc
  AttacherType = Attacher::AttachEngine3D
FEATURE [Part::Feature] Pcb_18fc
  Placement = pos=(-134.21,133.38,0) rot=(0,0,1;0rad)
  shape: bbox 60 x 100 x 1.6 mm, 67 faces (baked)
FEATURE [Sketcher::SketchObject] PCB_Sketch_18fc
  FullyConstrained = false
  sketch-geometry (9):
    g0: LineSegment StartX=60 StartY=100 StartZ=0 EndX=60 EndY=0 EndZ=0
    g1: LineSegment StartX=60 StartY=0 StartZ=0 EndX=0 EndY=0 EndZ=0
    g2: LineSegment StartX=0 StartY=100 StartZ=0 EndX=60 EndY=100 EndZ=0
    g3: LineSegment StartX=0 StartY=100 StartZ=0 EndX=0 EndY=0 EndZ=0
    g4: Circle CenterX=25.8 CenterY=95.8 CenterZ=0 NormalX=0 NormalY=0 NormalZ=1 AngleXU=0 Radius=2.2
    g5: Circle CenterX=25.8 CenterY=60.8 CenterZ=0 NormalX=0 NormalY=0 NormalZ=1 AngleXU=0 Radius=2.2
    g6: Circle CenterX=56.3 CenterY=78.3 CenterZ=0 NormalX=0 NormalY=0 NormalZ=1 AngleXU=0 Radius=1.7
    g7: Circle CenterX=55 CenterY=5 CenterZ=0 NormalX=0 NormalY=0 NormalZ=1 AngleXU=0 Radius=1.7
    g8: Circle CenterX=16 CenterY=5 CenterZ=0 NormalX=0 NormalY=0 NormalZ=1 AngleXU=0 Radius=1.7
  constraints (4):
    c: Coincident(g3,g1)
    c: Coincident(g2,g3)
    c: Coincident(g0,g1)
    c: Coincident(g2,g0)
FEATURE [App::Part] Board_Geoms_18fc
  Group = -> [Local_CS_18fc,Pcb_18fc,PCB_Sketch_18fc]
  Origin = -> Origin
FEATURE [Part::Feature] Shape  label="J4_JST_B8B_PH_K_61817312"
  Placement = pos=(49.9,29.5,-1.6) rot=(0.707107,-0.707107,0;3.14159rad)
  shape: bbox 4.55 x 17.9 x 9.4 mm, 261 faces (baked)
FEATURE [Part::Feature] Shape001  label="U1_ESP32-WROOM-32_6181740E"
  Placement = pos=(50,50,0) rot=(0,0,-1;1.5708rad)
  shape: bbox 25.5 x 18 x 3.1 mm, 751 faces (baked)
FEATURE [Part::Feature] Shape002  label="J5_JST_B5B_XH_A_61817515"
  Placement = pos=(4.4,47.1,-1.6) rot=(0.707107,0.707107,0;3.14159rad)
  shape: bbox 5.75 x 14.9 x 10.4 mm, 165 faces (baked)
FEATURE [Part::Feature] Shape003  label="U5_SOT_223_61818112"
  Placement = pos=(10.45,27.75,0) rot=(0,0,1;0rad)
  shape: bbox 7 x 6.5 x 1.7 mm, 78 faces (baked)
FEATURE [Part::Feature] Shape004  label="U3_SOT_23_6181763C"
  Placement = pos=(46.3,78.5,-1.6) rot=(1,0,0;3.14159rad)
  shape: bbox 2.5 x 3 x 1.2 mm, 76 faces (baked)
FEATURE [App::Part] Bot_18fc
  Group = -> [Shape,Shape002,Shape004]
  Origin = -> Origin004
FEATURE [Part::Feature] Shape005  label="U2_SOIC_18W_75x116mm_P127mm_6181850D"
  Placement = pos=(19.1,74.4,0) rot=(0,0,1;3.14159rad)
  shape: bbox 10.3 x 11.55 x 2.75 mm, 306 faces (baked)
FEATURE [Part::Feature] Shape006  label="SW2_User Library-PEC12-4220F-S0024-1_61817C63"
  Placement = pos=(32.1,26.9,0) rot=(0.57735,-0.57735,-0.57735;2.0944rad)
  shape: bbox 14.2 x 12.4 x 20.88 mm, 379 faces (baked)
FEATURE [Part::Feature] Shape007  label="R1_R_0805_2012Metric_61817EAB"
  Placement = pos=(26,3.3,0) rot=(0,0,1;1.5708rad)
  shape: bbox 1.2 x 2 x 0.45 mm, 26 faces (baked)
FEATURE [Part::Feature] Shape008  label="J3_BarrelJack_CUI_PJ-202A_Horizontal_7100000000.0"
  Placement = pos=(10,10.5,0) rot=(0,0,1;0rad)
  shape: bbox 14.48 x 9.573 x 14.73 mm, 706 faces, 3 solids (baked)
FEATURE [App::Link] J3_BarrelJack_CUI_PJ_202A_Horizontal_7100000000_0_ln_  label="J3_BarrelJack_CUI_PJ-202A_Horizontal_7100000000.0[2]"
  LinkPlacement = pos=(10,10.5,0) rot=(0,0,1;0rad)
  LinkedObject = -> Shape008
  Placement = pos=(10,10.5,0) rot=(0,0,1;0rad)
FEATURE [Part::Feature] Shape009  label="J2_IDC_Header_2x05_P254mm_Vertical_6181716A"
  Placement = pos=(16.2,52.2,0) rot=(0,0,1;0rad)
  shape: bbox 9.1 x 20.36 x 12.1 mm, 222 faces (baked)
FEATURE [Part::Feature] Shape010  label="J1_IDC_Header_2x03_P254mm_Vertical_61817595"
  Placement = pos=(37,5.5,0) rot=(0,0,1;1.5708rad)
  shape: bbox 15.28 x 9.1 x 12.1 mm, 150 faces (baked)
FEATURE [Part::Feature] Shape011  label="C5_C_0805_2012Metric_61817AE0"
  Placement = pos=(56.8,66.8,0) rot=(0,0,1;0rad)
  shape: bbox 2 x 1.25 x 1.25 mm, 28 faces (baked)
FEATURE [App::Link] C5_C_0805_2012Metric_61817AE0_ln_  label="C4_C_0805_2012Metric_61817AB0"
  LinkPlacement = pos=(56.9,63,0) rot=(0,0,1;0rad)
  LinkedObject = -> Shape011
  Placement = pos=(56.9,63,0) rot=(0,0,1;0rad)
FEATURE [App::Link] C5_C_0805_2012Metric_61817AE0_ln_001  label="C3_C_0805_2012Metric_618180DD"
  LinkPlacement = pos=(12.5,33,0) rot=(0,0,1;3.14159rad)
  LinkedObject = -> Shape011
  Placement = pos=(12.5,33,0) rot=(0,0,1;3.14159rad)
FEATURE [App::Link] C5_C_0805_2012Metric_61817AE0_ln_002  label="C2_C_0805_2012Metric_618180AD"
  LinkPlacement = pos=(8.3375,22.4,0) rot=(0,0,1;0rad)
  LinkedObject = -> Shape011
  Placement = pos=(8.3375,22.4,0) rot=(0,0,1;0rad)
FEATURE [App::Link] C5_C_0805_2012Metric_61817AE0_ln_003  label="C1_C_0805_2012Metric_61817E7B"
  LinkPlacement = pos=(26,9.4625,0) rot=(0,0,1;1.5708rad)
  LinkedObject = -> Shape011
  Placement = pos=(26,9.4625,0) rot=(0,0,1;1.5708rad)
FEATURE [App::Part] Top_18fc
  Group = -> [Shape001,Shape003,Shape005,Shape006,Shape007,Shape008,J3_BarrelJack_CUI_PJ_202A_Horizontal_7100000000_0_ln_,Shape009,Shape010,Shape011,C5_C_0805_2012Metric_61817AE0_ln_,C5_C_0805_2012Metric_61817AE0_ln_001,C5_C_0805_2012Metric_61817AE0_ln_002,C5_C_0805_2012Metric_61817AE0_ln_003]
  Origin = -> Origin003
FEATURE [App::Part] Step_Models_18fc
  Group = -> [Top_18fc,Bot_18fc]
  Origin = -> Origin002
FEATURE [PartDesign::CoordinateSystem] LCS_0  label="LCS_mount1"
  AttacherType = Attacher::AttachEngine3D
  MapMode = 11
  Placement = pos=(16,5,-1.6) rot=(0,0,1;1.5708rad)
  Support = -> [Pcb_18fc]
FEATURE [PartDesign::CoordinateSystem] LCS_knob
  AttacherType = Attacher::AttachEngine3D
  MapMode = 11
  Placement = pos=(32.1,26.9,12.3) rot=(0,0,1;2.15523rad)
  Support = -> [Shape006]
FEATURE [App::Part] Board_18fc  label="PCB"
  Group = -> [Board_Geoms_18fc,Step_Models_18fc,LCS_0,LCS_knob]
  Origin = -> Origin001
---- part knob.FCStd = doc fcstd_76f986f2526c ----
FCSTD DOCUMENT  (FreeCAD 0.19R24291 (Git))
Label: knob
License: All rights reserved
LicenseURL: http://en.wikipedia.org/wiki/All_rights_reserved
objects: Sketcher::SketchObject×4, PartDesign::CoordinateSystem×2, PartDesign::Pocket×2, PartDesign::Revolution×1, PartDesign::Body×1
note: 13 computed .brp shape members not serialized (recipe doc carries the construction recipe); baked Part::Feature solids carry a one-line shape summary decoded from their .brp
EXTERNAL_REF file=data.FCStd obj=Spreadsheet

FEATURE [PartDesign::CoordinateSystem] LCS_0
  AttacherType = Attacher::AttachEngine3D
  MapMode = 2
  Support = -> [X_Axis]
FEATURE [Sketcher::SketchObject] Sketch_knob
  FullyConstrained = true
  MapMode = 5
  Placement = pos=(0,0,0) rot=(1,0,0;1.5708rad)
  Support = -> [XZ_Plane]
  expr: Constraints[11] = data#<<data>>.KnobShaftOutsideDiameter / 2
  expr: Constraints[12] = data#<<data>>.KnobShaftLength
  expr: Constraints[24] = data#<<data>>.KnobHeight
  expr: Constraints[15] = data#<<data>>.KnobCornerRadius
  expr: Constraints[18] = data#<<data>>.KnobDiameter / 2
  sketch-geometry (8):
    g0: LineSegment StartX=0 StartY=0 StartZ=0 EndX=0 EndY=15.6 EndZ=0
    g1: LineSegment StartX=0 StartY=15.6 StartZ=0 EndX=11 EndY=15.6 EndZ=0
    g2: LineSegment StartX=12 StartY=14.6 StartZ=0 EndX=12 EndY=6.6 EndZ=0
    g3: LineSegment StartX=11 StartY=5.6 StartZ=0 EndX=5 EndY=5.6 EndZ=0
    g4: LineSegment StartX=5 StartY=5.6 StartZ=0 EndX=5 EndY=0 EndZ=0
    g5: LineSegment StartX=5 StartY=0 StartZ=0 EndX=0 EndY=0 EndZ=0
    g6: ArcOfCircle CenterX=11 CenterY=14.6 CenterZ=0 NormalX=0 NormalY=0 NormalZ=1 AngleXU=0 Radius=1 StartAngle=0 EndAngle=1.5708
    g7: ArcOfCircle CenterX=11 CenterY=6.6 CenterZ=0 NormalX=0 NormalY=0 NormalZ=1 AngleXU=0 Radius=1 StartAngle=4.71239 EndAngle=6.28319
  constraints (25):
    c: Vertical(g0)
    c: Coincident(g0,g1)
    c: Horizontal(g1)
    c: Vertical(g2)
    c: Horizontal(g3)
    c: Coincident(g3,g4)
    c: Vertical(g4)
    c: Coincident(g4,g5)
    c: Coincident(g5,g0)
    c: Horizontal(g5)
    c: Coincident(g0,g-1)
    c: DistanceX(g5,g5) = 5
    c: DistanceY(g4,g4) = 5.6
    c: Vertical(g6,g6)
    c: Horizontal(g6,g6)
    c: Radius(g6) = 1
    c: Coincident(g6,g2)
    c: Coincident(g1,g6)
    c: DistanceX(g0,g2) = 12
    c: Equal(g7,g6)
    c: Horizontal(g7,g7)
    c: Vertical(g7,g7)
    c: Coincident(g2,g7)
    c: Coincident(g7,g3)
    c: DistanceY(g3,g1) = 10
FEATURE [PartDesign::Revolution] Revolution
  Angle = 360
  Axis = (0,-2e-16,1)
  Base = (0,0,0)
  Placement = pos=(0,0,0) rot=(1,0,0;1.5708rad)
  Profile = -> Sketch_knob
  ReferenceAxis = -> Sketch_knob [V_Axis]
FEATURE [Sketcher::SketchObject] Sketch
  FullyConstrained = true
  MapMode = 5
  Support = -> [XY_Plane]
  expr: Constraints[3] = data#<<data>>.KnobShaftCut
  expr: Constraints[1] = data#<<data>>.KnobShaftDiameter
  sketch-geometry (2):
    g0: ArcOfCircle CenterX=0 CenterY=0 CenterZ=0 NormalX=0 NormalY=0 NormalZ=1 AngleXU=0 Radius=3.2 StartAngle=2.65372 EndAngle=6.77106
    g1: LineSegment StartX=-2.82666 StartY=1.5 StartZ=0 EndX=2.82666 EndY=1.5 EndZ=0
  constraints (6):
    c: Coincident(g0,g-1)
    c: Diameter(g0) = 6.4
    c: Horizontal(g1)
    c: DistanceY(g0,g1) = 1.5
    c: Coincident(g0,g1)
    c: Coincident(g0,g1)
FEATURE [PartDesign::Pocket] Pocket
  BaseFeature = -> Revolution
  Length = 12
  Length2 = 100
  Placement = pos=(0,0,0) rot=(1,0,0;1.5708rad)
  Profile = -> Sketch
  Reversed = true
  Type = 0
  expr: Length = data#<<data>>.KnobShaftDepth
FEATURE [Sketcher::SketchObject] Sketch001
  FullyConstrained = true
  MapMode = 5
  Support = -> [XY_Plane]
  expr: Constraints[1] = data#<<data>>.KnobShaftDiameter2
  sketch-geometry (1):
    g0: Circle CenterX=0 CenterY=0 CenterZ=0 NormalX=0 NormalY=0 NormalZ=1 AngleXU=0 Radius=3.5
  constraints (2):
    c: Coincident(g0,g-1)
    c: Diameter(g0) = 7
FEATURE [PartDesign::Pocket] Pocket001
  BaseFeature = -> Pocket
  Length = 4.5
  Length2 = 100
  Placement = pos=(0,0,0) rot=(1,0,0;1.5708rad)
  Profile = -> Sketch001
  Reversed = true
  Type = 0
  expr: Length = data#<<data>>.KnobShaftDepth2
FEATURE [PartDesign::CoordinateSystem] LCS_encoder
  AttacherType = Attacher::AttachEngine3D
  MapMode = 11
  Placement = pos=(0,0,4.5) rot=(0.707107,-0.707107,0;3.14159rad)
  Support = -> [Pocket001]
FEATURE [Sketcher::SketchObject] Sketch002
  FullyConstrained = true
  MapMode = 5
  Placement = pos=(0,0,0) rot=(1,0,0;1.5708rad)
  Support = -> [XZ_Plane]
  expr: Constraints[10] = data#<<data>>.KnobDiameter / 2
  expr: Constraints[11] = data#<<data>>.KnobShaftLength
  sketch-geometry (4):
    g0: LineSegment StartX=12 StartY=7.01421 StartZ=0 EndX=10.5858 EndY=5.6 EndZ=0
    g1: LineSegment StartX=10.5858 StartY=5.6 StartZ=0 EndX=12 EndY=4.18579 EndZ=0
    g2: LineSegment StartX=13.4142 StartY=5.6 StartZ=0 EndX=12 EndY=4.18579 EndZ=0
    g3: LineSegment StartX=12 StartY=7.01421 StartZ=0 EndX=13.4142 EndY=5.6 EndZ=0
  constraints (12):
    c: Coincident(g0,g1)
    c: Vertical(g0,g1)
    c: Coincident(g2,g1)
    c: Equal(g0,g1)
    c: Equal(g1,g2)
    c: Coincident(g3,g0)
    c: Coincident(g3,g2)
    c: Horizontal(g0,g2)
    c: Distance(g3) = 2
    c: Perpendicular(g3,g2)
    c: DistanceX(g-1,g1) = 12
    c: DistanceY(g-1,g0) = 5.6
FEATURE [PartDesign::Body] Body_knob
  Group = -> [LCS_0,Sketch_knob,Revolution,Sketch,Pocket,Sketch001,Pocket001,LCS_encoder,Sketch002]
  Origin = -> Origin
  Tip = -> Pocket001
